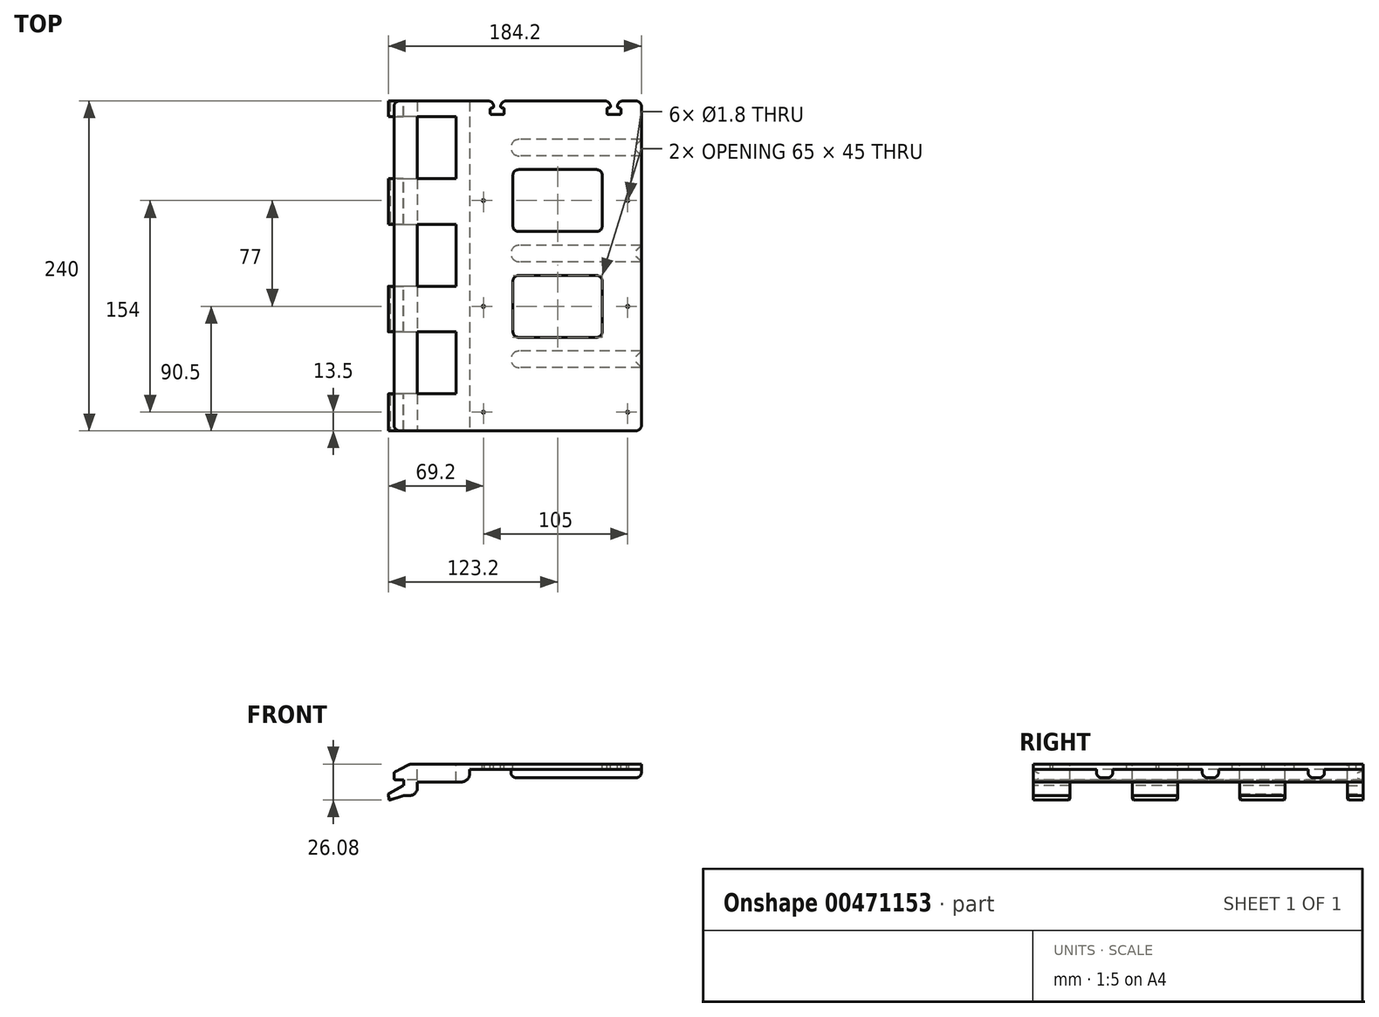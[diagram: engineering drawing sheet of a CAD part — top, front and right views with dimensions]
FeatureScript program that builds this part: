
annotation { "Feature Type Name" : "Feature", "Feature Type Description" : "" }
export const myFeature = defineFeature(function(context is Context, id is Id, definition is map)
    precondition{}
    {
        {
            var Q0;
            Q0=qCreatedBy(makeId("Top.planeOp"),FACE);
            var sketch = newSketch(context, id + "F0", { "sketchPlane" : qUnion([Q0])});
            skLineSegment(sketch, "E0", {"start": v(0, -188) * mm, "end": v(180, -188) * mm, "construction": true});
            skLineSegment(sketch, "E1", {"start": v(0, -34) * mm, "end": v(180, -34) * mm, "construction": true});
            skLineSegment(sketch, "E2", {"start": v(0, -149.5) * mm, "end": v(180, -149.5) * mm, "construction": true});
            skLineSegment(sketch, "E3", {"start": v(0, -72.5) * mm, "end": v(180, -72.5) * mm, "construction": true});
            skLineSegment(sketch, "E4", {"start": v(180, -194) * mm, "end": v(91, -194) * mm});
            skLineSegment(sketch, "E5", {"start": v(180, -182) * mm, "end": v(91, -182) * mm});
            skArc(sketch, "E6", {"start": v(91, -182) * mm, "mid": v(85, -188) * mm, "end": v(91, -194) * mm});
            skLineSegment(sketch, "E7", {"start": v(180, -117) * mm, "end": v(91, -117) * mm});
            skLineSegment(sketch, "E8", {"start": v(180, -105) * mm, "end": v(91, -105) * mm});
            skArc(sketch, "E9", {"start": v(91, -105) * mm, "mid": v(85, -111) * mm, "end": v(91, -117) * mm});
            skLineSegment(sketch, "E10", {"start": v(180, -40) * mm, "end": v(91, -40) * mm});
            skLineSegment(sketch, "E11", {"start": v(180, -28) * mm, "end": v(91, -28) * mm});
            skArc(sketch, "E12", {"start": v(91, -28) * mm, "mid": v(85, -34) * mm, "end": v(91, -40) * mm});
            skLineSegment(sketch, "E13", {"start": v(91, -240) * mm, "end": v(91, 0) * mm, "construction": true});
            skCircle(sketch, "E14", {"center": v(65, -149.5) * mm, "radius": 0.9 * mm});
            skCircle(sketch, "E15", {"center": v(65, -72.5) * mm, "radius": 0.9 * mm});
            skCircle(sketch, "E16", {"center": v(170, -149.5) * mm, "radius": 0.9 * mm});
            skCircle(sketch, "E17", {"center": v(170, -72.5) * mm, "radius": 0.9 * mm});
            skLineSegment(sketch, "E18.bottom", {"start": v(180, -240) * mm, "end": v(0, -240) * mm});
            skLineSegment(sketch, "E18.top", {"start": v(180, 0) * mm, "end": v(0, 0) * mm});
            skLineSegment(sketch, "E18.left", {"start": v(180, -240) * mm, "end": v(180, 0) * mm});
            skLineSegment(sketch, "E18.right", {"start": v(0, -240) * mm, "end": v(0, 0) * mm});
            skLineSegment(sketch, "E19", {"start": v(5, 0) * mm, "end": v(5, -240) * mm});
            skLineSegment(sketch, "E20", {"start": v(17, 0) * mm, "end": v(17, -240) * mm});
            skLineSegment(sketch, "E21", {"start": v(55, 0) * mm, "end": v(55, -240) * mm});
            skLineSegment(sketch, "E22", {"start": v(0, -89.7) * mm, "end": v(45, -89.7) * mm});
            skLineSegment(sketch, "E23", {"start": v(45, -89.7) * mm, "end": v(45, -134.9) * mm});
            skLineSegment(sketch, "E24", {"start": v(45, -134.9) * mm, "end": v(0, -134.9) * mm});
            skLineSegment(sketch, "E25", {"start": v(0, -168) * mm, "end": v(45, -168) * mm});
            skLineSegment(sketch, "E26", {"start": v(45, -168) * mm, "end": v(45, -213.2) * mm});
            skLineSegment(sketch, "E27", {"start": v(45, -213.2) * mm, "end": v(0, -213.2) * mm});
            skLineSegment(sketch, "E28", {"start": v(0, -56.6) * mm, "end": v(45, -56.6) * mm});
            skLineSegment(sketch, "E29", {"start": v(45, -56.6) * mm, "end": v(45, -11.4) * mm});
            skLineSegment(sketch, "E30", {"start": v(45, -11.4) * mm, "end": v(0, -11.4) * mm});
            skLineSegment(sketch, "E31", {"start": v(0, -226.5) * mm, "end": v(180, -226.5) * mm, "construction": true});
            skCircle(sketch, "E32", {"center": v(65, -226.5) * mm, "radius": 0.9 * mm});
            skCircle(sketch, "E33", {"center": v(170, -226.5) * mm, "radius": 0.9 * mm});
            skLineSegment(sketch, "E34.bottom", {"start": v(151.5, -95) * mm, "end": v(86.5, -95) * mm});
            skLineSegment(sketch, "E34.top", {"start": v(151.5, -50) * mm, "end": v(86.5, -50) * mm});
            skLineSegment(sketch, "E34.left", {"start": v(151.5, -95) * mm, "end": v(151.5, -50) * mm});
            skLineSegment(sketch, "E34.right", {"start": v(86.5, -95) * mm, "end": v(86.5, -50) * mm});
            skPoint(sketch, "E34.middle", {"position": v(119, -72.5) * mm});
            skLineSegment(sketch, "E35.bottom", {"start": v(151.5, -172) * mm, "end": v(86.5, -172) * mm});
            skLineSegment(sketch, "E35.top", {"start": v(151.5, -127) * mm, "end": v(86.5, -127) * mm});
            skLineSegment(sketch, "E35.left", {"start": v(151.5, -172) * mm, "end": v(151.5, -127) * mm});
            skLineSegment(sketch, "E35.right", {"start": v(86.5, -172) * mm, "end": v(86.5, -127) * mm});
            skPoint(sketch, "E35.middle", {"position": v(119, -149.5) * mm});
            skPoint(sketch, "E36.centerSnap0", {"position": v(119, -172) * mm});
            skLineSegment(sketch, "E37", {"start": v(91, -111) * mm, "end": v(180, -111) * mm, "construction": true});
            skLineSegment(sketch, "E38", {"start": v(91, -111) * mm, "end": v(0, -111) * mm, "construction": true});
            skLineSegment(sketch, "E39.bottom", {"start": v(157.5, 0) * mm, "end": v(162.5, 0) * mm});
            skLineSegment(sketch, "E39.top", {"start": v(157.5, -5) * mm, "end": v(162.5, -5) * mm});
            skLineSegment(sketch, "E39.left", {"start": v(157.5, 0) * mm, "end": v(157.5, -5) * mm});
            skLineSegment(sketch, "E39.right", {"start": v(162.5, 0) * mm, "end": v(162.5, -5) * mm});
            skLineSegment(sketch, "E40.bottom", {"start": v(72.5, 0) * mm, "end": v(77.5, 0) * mm});
            skLineSegment(sketch, "E40.top", {"start": v(72.5, -5) * mm, "end": v(77.5, -5) * mm});
            skLineSegment(sketch, "E40.left", {"start": v(72.5, 0) * mm, "end": v(72.5, -5) * mm});
            skLineSegment(sketch, "E40.right", {"start": v(77.5, 0) * mm, "end": v(77.5, -5) * mm});
            skLineSegment(sketch, "E41", {"start": v(75, -5) * mm, "end": v(75, -34) * mm, "construction": true});
            skLineSegment(sketch, "E42", {"start": v(160, -5) * mm, "end": v(160, -34) * mm, "construction": true});
            skLineSegment(sketch, "E43.bottom", {"start": v(70, -5) * mm, "end": v(80, -5) * mm});
            skLineSegment(sketch, "E43.top", {"start": v(70, -10) * mm, "end": v(80, -10) * mm});
            skLineSegment(sketch, "E43.left", {"start": v(70, -5) * mm, "end": v(70, -10) * mm});
            skLineSegment(sketch, "E43.right", {"start": v(80, -5) * mm, "end": v(80, -10) * mm});
            skLineSegment(sketch, "E44.bottom", {"start": v(155, -5) * mm, "end": v(165, -5) * mm});
            skLineSegment(sketch, "E44.top", {"start": v(155, -10) * mm, "end": v(165, -10) * mm});
            skLineSegment(sketch, "E44.left", {"start": v(155, -5) * mm, "end": v(155, -10) * mm});
            skLineSegment(sketch, "E44.right", {"start": v(165, -5) * mm, "end": v(165, -10) * mm});
            skLineSegment(sketch, "E45.bottom", {"start": v(152.5, -240) * mm, "end": v(147.5, -240) * mm});
            skSolve(sketch);
        }
        {
            var Q0;
            {var subQ7=sQuery(id+"F0.wireOp",EDGE,"E4");Q0=makeQuery(id+"F0.imprint","IMPRINT",FACE,{"disambiguationData":[TD([[makeQuery(id+"F0.imprint","IMPRINT",EDGE,{"derivedFrom":subQ7}),1.0]])]});}
            var Q1;
            {var subQ0=sQuery(id+"F0.wireOp",EDGE,"E4");Q1=makeQuery(id+"F0.imprint","IMPRINT",FACE,{"disambiguationData":[TD([[makeQuery(id+"F0.imprint","IMPRINT",EDGE,{"derivedFrom":subQ0}),-1.0]])]});}
            var Q2;
            {var subQ0=sQuery(id+"F0.wireOp",EDGE,"E7");Q2=makeQuery(id+"F0.imprint","IMPRINT",FACE,{"disambiguationData":[TD([[makeQuery(id+"F0.imprint","IMPRINT",EDGE,{"derivedFrom":subQ0}),-1.0]])]});}
            var Q3;
            {var subQ0=sQuery(id+"F0.wireOp",EDGE,"E10");Q3=makeQuery(id+"F0.imprint","IMPRINT",FACE,{"disambiguationData":[TD([[makeQuery(id+"F0.imprint","IMPRINT",EDGE,{"derivedFrom":subQ0}),-1.0]])]});}
            extrude(context, id + "F1", {"entities" : qUnion([Q0, Q1, Q2, Q3]), "oppositeDirection" : true, "depth" : 4 * mm});
        }
        {
            var Q0;
            {var subQ0=sQuery(id+"F0.wireOp",EDGE,"E20");Q0=makeQuery(id+"F0.imprint","IMPRINT",FACE,{"disambiguationData":[TD([[makeQuery(id+"F0.imprint","IMPRINT",EDGE,{"derivedFrom":subQ0}),1.0]])]});}
            var Q1;
            {var subQ5=sQuery(id+"F0.wireOp",EDGE,"n4lQ4PQO-9XsQ-tz0W-XekK-HpTfJCge4sbG");Q1=makeQuery(id+"F0.imprint","IMPRINT",FACE,{"disambiguationData":[TD([[makeQuery(id+"F0.imprint","IMPRINT",EDGE,{"derivedFrom":subQ5}),1.0]])]});}
            var Q2;
            {var subQ5=sQuery(id+"F0.wireOp",EDGE,"NRY2d1nv-D3un-2PJu-Z2eF-jLOu5DY2E8th");Q2=makeQuery(id+"F0.imprint","IMPRINT",FACE,{"disambiguationData":[TD([[makeQuery(id+"F0.imprint","IMPRINT",EDGE,{"derivedFrom":subQ5}),1.0]])]});}
            extrude(context, id + "F2", {"entities" : qUnion([Q0, Q1, Q2]), "operationType" : NewBodyOperationType.ADD, "oppositeDirection" : true, "depth" : 13 * mm});
        }
        {
            var Q0;
            {var subQ0=sQuery(id+"F0.wireOp",EDGE,"E19");var subQ1=sQuery(id+"F0.wireOp",EDGE,"E18.bottom");var subQ2=makeQuery(id+"F0.imprint","INTERSECT",VERTEX,{"derivedFrom":[subQ1,subQ0]});Q0=makeQuery(id+"F0.imprint","IMPRINT",FACE,{"disambiguationData":[TD([[makeQuery(id+"F0.imprint","IMPRINT",EDGE,{"disambiguationData":[TD([[subQ2,1.0]])],"derivedFrom":subQ1}),-1.0]])]});}
            var Q1;
            {var subQ0=sQuery(id+"F0.wireOp",EDGE,"E19");var subQ1=sQuery(id+"F0.wireOp",EDGE,"E18.top");var subQ2=makeQuery(id+"F0.imprint","INTERSECT",VERTEX,{"derivedFrom":[subQ1,subQ0]});Q1=makeQuery(id+"F0.imprint","IMPRINT",FACE,{"disambiguationData":[TD([[makeQuery(id+"F0.imprint","IMPRINT",EDGE,{"disambiguationData":[TD([[subQ2,1.0]])],"derivedFrom":subQ1}),1.0]])]});}
            var Q2;
            {var subQ0=sQuery(id+"F0.wireOp",EDGE,"E28");var subQ1=sQuery(id+"F0.wireOp",EDGE,"E19");var subQ2=makeQuery(id+"F0.imprint","INTERSECT",VERTEX,{"derivedFrom":[subQ1,subQ0]});Q2=makeQuery(id+"F0.imprint","IMPRINT",FACE,{"disambiguationData":[TD([[makeQuery(id+"F0.imprint","IMPRINT",EDGE,{"disambiguationData":[TD([[subQ2,-1.0]])],"derivedFrom":subQ1}),1.0]])]});}
            var Q3;
            {var subQ0=sQuery(id+"F0.wireOp",EDGE,"E24");var subQ1=sQuery(id+"F0.wireOp",EDGE,"E19");var subQ2=makeQuery(id+"F0.imprint","INTERSECT",VERTEX,{"derivedFrom":[subQ1,subQ0]});Q3=makeQuery(id+"F0.imprint","IMPRINT",FACE,{"disambiguationData":[TD([[makeQuery(id+"F0.imprint","IMPRINT",EDGE,{"disambiguationData":[TD([[subQ2,-1.0]])],"derivedFrom":subQ1}),1.0]])]});}
            extrude(context, id + "F3", {"entities" : qUnion([Q0, Q1, Q2, Q3]), "operationType" : NewBodyOperationType.ADD, "oppositeDirection" : true, "depth" : 23 * mm});
        }
        {
            var Q0;
            {var subQ0=sQuery(id+"F0.wireOp",EDGE,"E18.right");var subQ1=sQuery(id+"F0.wireOp",EDGE,"E18.bottom");var subQ2=makeQuery(id+"F0.imprint","INTERSECT",VERTEX,{"derivedFrom":[subQ1,subQ0]});Q0=makeQuery(id+"F0.imprint","IMPRINT",FACE,{"disambiguationData":[TD([[makeQuery(id+"F0.imprint","IMPRINT",EDGE,{"disambiguationData":[TD([[subQ2,1.0]])],"derivedFrom":subQ1}),-1.0]])]});}
            var Q1;
            {var subQ0=sQuery(id+"F0.wireOp",EDGE,"E18.right");var subQ1=sQuery(id+"F0.wireOp",EDGE,"E18.top");var subQ2=makeQuery(id+"F0.imprint","INTERSECT",VERTEX,{"derivedFrom":[subQ1,subQ0]});Q1=makeQuery(id+"F0.imprint","IMPRINT",FACE,{"disambiguationData":[TD([[makeQuery(id+"F0.imprint","IMPRINT",EDGE,{"disambiguationData":[TD([[subQ2,1.0]])],"derivedFrom":subQ1}),1.0]])]});}
            var Q2;
            {var subQ0=sQuery(id+"F0.wireOp",EDGE,"E24");var subQ1=sQuery(id+"F0.wireOp",EDGE,"E18.right");var subQ2=makeQuery(id+"F0.imprint","INTERSECT",VERTEX,{"derivedFrom":[subQ1,subQ0]});Q2=makeQuery(id+"F0.imprint","IMPRINT",FACE,{"disambiguationData":[TD([[makeQuery(id+"F0.imprint","IMPRINT",EDGE,{"disambiguationData":[TD([[subQ2,1.0]])],"derivedFrom":subQ1}),-1.0]])]});}
            var Q3;
            {var subQ0=sQuery(id+"F0.wireOp",EDGE,"E22");var subQ1=sQuery(id+"F0.wireOp",EDGE,"E18.right");var subQ2=makeQuery(id+"F0.imprint","INTERSECT",VERTEX,{"derivedFrom":[subQ1,subQ0]});Q3=makeQuery(id+"F0.imprint","IMPRINT",FACE,{"disambiguationData":[TD([[makeQuery(id+"F0.imprint","IMPRINT",EDGE,{"disambiguationData":[TD([[subQ2,-1.0]])],"derivedFrom":subQ1}),-1.0]])]});}
            var Q4;
            {var subQ0=sQuery(id+"F0.wireOp",EDGE,"E25");var subQ1=sQuery(id+"F0.wireOp",EDGE,"E18.right");var subQ2=makeQuery(id+"F0.imprint","INTERSECT",VERTEX,{"derivedFrom":[subQ1,subQ0]});Q4=makeQuery(id+"F0.imprint","IMPRINT",FACE,{"disambiguationData":[TD([[makeQuery(id+"F0.imprint","IMPRINT",EDGE,{"disambiguationData":[TD([[subQ2,1.0]])],"derivedFrom":subQ1}),-1.0]])]});}
            var Q5;
            {var subQ0=sQuery(id+"F0.wireOp",EDGE,"E22");var subQ1=sQuery(id+"F0.wireOp",EDGE,"E18.right");var subQ2=makeQuery(id+"F0.imprint","INTERSECT",VERTEX,{"derivedFrom":[subQ1,subQ0]});Q5=makeQuery(id+"F0.imprint","IMPRINT",FACE,{"disambiguationData":[TD([[makeQuery(id+"F0.imprint","IMPRINT",EDGE,{"disambiguationData":[TD([[subQ2,1.0]])],"derivedFrom":subQ1}),-1.0]])]});}
            var Q6;
            {var subQ0=sQuery(id+"F0.wireOp",EDGE,"E28");var subQ1=sQuery(id+"F0.wireOp",EDGE,"E18.right");var subQ2=makeQuery(id+"F0.imprint","INTERSECT",VERTEX,{"derivedFrom":[subQ1,subQ0]});Q6=makeQuery(id+"F0.imprint","IMPRINT",FACE,{"disambiguationData":[TD([[makeQuery(id+"F0.imprint","IMPRINT",EDGE,{"disambiguationData":[TD([[subQ2,-1.0]])],"derivedFrom":subQ1}),-1.0]])]});}
            var Q7;
            {var subQ0=sQuery(id+"F0.wireOp",EDGE,"E25");var subQ1=sQuery(id+"F0.wireOp",EDGE,"E19");var subQ2=makeQuery(id+"F0.imprint","INTERSECT",VERTEX,{"derivedFrom":[subQ1,subQ0]});Q7=makeQuery(id+"F0.imprint","IMPRINT",FACE,{"disambiguationData":[TD([[makeQuery(id+"F0.imprint","IMPRINT",EDGE,{"disambiguationData":[TD([[subQ2,-1.0]])],"derivedFrom":subQ1}),1.0]])]});}
            var Q8;
            {var subQ0=sQuery(id+"F0.wireOp",EDGE,"E22");var subQ1=sQuery(id+"F0.wireOp",EDGE,"E19");var subQ2=makeQuery(id+"F0.imprint","INTERSECT",VERTEX,{"derivedFrom":[subQ1,subQ0]});Q8=makeQuery(id+"F0.imprint","IMPRINT",FACE,{"disambiguationData":[TD([[makeQuery(id+"F0.imprint","IMPRINT",EDGE,{"disambiguationData":[TD([[subQ2,-1.0]])],"derivedFrom":subQ1}),1.0]])]});}
            var Q9;
            {var subQ0=sQuery(id+"F0.wireOp",EDGE,"E30");var subQ1=sQuery(id+"F0.wireOp",EDGE,"E19");var subQ2=makeQuery(id+"F0.imprint","INTERSECT",VERTEX,{"derivedFrom":[subQ1,subQ0]});Q9=makeQuery(id+"F0.imprint","IMPRINT",FACE,{"disambiguationData":[TD([[makeQuery(id+"F0.imprint","IMPRINT",EDGE,{"disambiguationData":[TD([[subQ2,-1.0]])],"derivedFrom":subQ1}),1.0]])]});}
            var Q10;
            Q10=makeQuery(id+"F2.opExtrude","CAP_FACE",FACE,{"disambiguationData":[OSD([sQuery(id+"F0.wireOp",EDGE,"E14"),sQuery(id+"F0.wireOp",EDGE,"E15"),sQuery(id+"F0.wireOp",EDGE,"E18.bottom"),sQuery(id+"F0.wireOp",EDGE,"E18.top"),sQuery(id+"F0.wireOp",EDGE,"E20"),sQuery(id+"F0.wireOp",EDGE,"E21")])],"isStart":false});
            extrude(context, id + "F4", {"entities" : qUnion([Q0, Q1, Q2, Q3, Q4, Q5, Q6, Q7, Q8, Q9]), "operationType" : NewBodyOperationType.ADD, "oppositeDirection" : true, "endBoundEntityFace" : qUnion([Q10]), "depth" : 11.5 * mm});
        }
        {
            var Q0;
            {var subQ0=sQuery(id+"F0.wireOp",EDGE,"E18.bottom");Q0=makeQuery(id+"F4.boolean.opBoolean","MERGE",FACE,{"derivedFrom":[makeQuery(id+"F3.boolean.opBoolean","MERGE",FACE,{"derivedFrom":[makeQuery(id+"F2.boolean.opBoolean","MERGE",FACE,{"derivedFrom":[makeQuery(id+"F1.opExtrude","SWEPT_FACE",FACE,{"disambiguationData":[OSD([subQ0])]}),makeQuery(id+"F2.opExtrude","SWEPT_FACE",FACE,{"disambiguationData":[OSD([subQ0])]})]}),makeQuery(id+"F3.opExtrude","SWEPT_FACE",FACE,{"disambiguationData":[OSD([subQ0])]})]}),makeQuery(id+"F4.opExtrude","SWEPT_FACE",FACE,{"disambiguationData":[OSD([subQ0])]})]});}
            var sketch = newSketch(context, id + "F5", { "sketchPlane" : qUnion([Q0])});
            skLineSegment(sketch, "E46.bottom", {"start": v(5, -11.5) * mm, "end": v(7, -11.5) * mm});
            skLineSegment(sketch, "E46.top", {"start": v(5, -15.5) * mm, "end": v(7, -15.5) * mm});
            skLineSegment(sketch, "E46.left", {"start": v(5, -11.5) * mm, "end": v(5, -15.5) * mm});
            skLineSegment(sketch, "E46.right", {"start": v(7, -11.5) * mm, "end": v(7, -15.5) * mm});
            skSolve(sketch);
        }
        {
            var Q0;
            Q0=makeQuery(id+"F5.imprint","IMPRINT",FACE,{"disambiguationData":[TD([[makeQuery(id+"F5.imprint","IMPRINT",EDGE,{"derivedFrom":sQuery(id+"F5.wireOp",EDGE,"E46.bottom")}),-1.0]])]});
            var Q1;
            {var subQ0=sQuery(id+"F0.wireOp",EDGE,"E18.top");Q1=makeQuery(id+"F4.boolean.opBoolean","MERGE",FACE,{"derivedFrom":[makeQuery(id+"F3.boolean.opBoolean","MERGE",FACE,{"derivedFrom":[makeQuery(id+"F2.boolean.opBoolean","MERGE",FACE,{"derivedFrom":[makeQuery(id+"F1.opExtrude","SWEPT_FACE",FACE,{"disambiguationData":[OSD([subQ0])]}),makeQuery(id+"F2.opExtrude","SWEPT_FACE",FACE,{"disambiguationData":[OSD([subQ0])]})]}),makeQuery(id+"F3.opExtrude","SWEPT_FACE",FACE,{"disambiguationData":[OSD([subQ0])]})]}),makeQuery(id+"F4.opExtrude","SWEPT_FACE",FACE,{"disambiguationData":[OSD([subQ0])]})]});}
            extrude(context, id + "F6", {"entities" : qUnion([Q0]), "operationType" : NewBodyOperationType.REMOVE, "oppositeDirection" : true, "endBoundEntityFace" : qUnion([Q1]), "depth" : 300 * mm});
        }
        {
            var Q0;
            {var subQ0=sQuery(id+"F0.wireOp",EDGE,"E4");Q0=makeQuery(id+"F0.imprint","IMPRINT",FACE,{"disambiguationData":[TD([[makeQuery(id+"F0.imprint","IMPRINT",EDGE,{"derivedFrom":subQ0}),-1.0]])]});}
            var Q1;
            {var subQ0=sQuery(id+"F0.wireOp",EDGE,"E7");Q1=makeQuery(id+"F0.imprint","IMPRINT",FACE,{"disambiguationData":[TD([[makeQuery(id+"F0.imprint","IMPRINT",EDGE,{"derivedFrom":subQ0}),-1.0]])]});}
            var Q2;
            {var subQ0=sQuery(id+"F0.wireOp",EDGE,"E10");Q2=makeQuery(id+"F0.imprint","IMPRINT",FACE,{"disambiguationData":[TD([[makeQuery(id+"F0.imprint","IMPRINT",EDGE,{"derivedFrom":subQ0}),-1.0]])]});}
            extrude(context, id + "F7", {"entities" : qUnion([Q0, Q1, Q2]), "operationType" : NewBodyOperationType.ADD, "oppositeDirection" : true, "depth" : 10 * mm});
        }
        {
            var Q0;
            Q0=makeQuery(id+"F7.opExtrude","CAP_FACE",FACE,{"disambiguationData":[OSD([sQuery(id+"F0.wireOp",EDGE,"E10"),sQuery(id+"F0.wireOp",EDGE,"E11"),sQuery(id+"F0.wireOp",EDGE,"E12"),sQuery(id+"F0.wireOp",EDGE,"E18.left")])],"isStart":false});
            var Q1;
            Q1=makeQuery(id+"F7.opExtrude","CAP_FACE",FACE,{"disambiguationData":[OSD([sQuery(id+"F0.wireOp",EDGE,"E7"),sQuery(id+"F0.wireOp",EDGE,"E8"),sQuery(id+"F0.wireOp",EDGE,"E9"),sQuery(id+"F0.wireOp",EDGE,"E18.left")])],"isStart":false});
            var Q2;
            Q2=makeQuery(id+"F7.opExtrude","CAP_FACE",FACE,{"disambiguationData":[OSD([sQuery(id+"F0.wireOp",EDGE,"E4"),sQuery(id+"F0.wireOp",EDGE,"E5"),sQuery(id+"F0.wireOp",EDGE,"E6"),sQuery(id+"F0.wireOp",EDGE,"E18.left")])],"isStart":false});
            var Q3;
            Q3=makeQuery(id+"F1.opExtrude","SWEPT_EDGE",EDGE,{"disambiguationData":[OSD([sQuery(id+"F0.wireOp",EDGE,"E34.top"),sQuery(id+"F0.wireOp",EDGE,"E34.right")])]});
            var Q4;
            Q4=makeQuery(id+"F1.opExtrude","SWEPT_EDGE",EDGE,{"disambiguationData":[OSD([sQuery(id+"F0.wireOp",EDGE,"E34.bottom"),sQuery(id+"F0.wireOp",EDGE,"E34.right")])]});
            var Q5;
            Q5=makeQuery(id+"F1.opExtrude","SWEPT_EDGE",EDGE,{"disambiguationData":[OSD([sQuery(id+"F0.wireOp",EDGE,"E34.top"),sQuery(id+"F0.wireOp",EDGE,"E34.left")])]});
            var Q6;
            Q6=makeQuery(id+"F1.opExtrude","SWEPT_EDGE",EDGE,{"disambiguationData":[OSD([sQuery(id+"F0.wireOp",EDGE,"E34.bottom"),sQuery(id+"F0.wireOp",EDGE,"E34.left")])]});
            var Q7;
            Q7=makeQuery(id+"F1.opExtrude","SWEPT_EDGE",EDGE,{"disambiguationData":[OSD([sQuery(id+"F0.wireOp",EDGE,"E35.top"),sQuery(id+"F0.wireOp",EDGE,"E35.left")])]});
            var Q8;
            {var subQ0=sQuery(id+"F0.wireOp",EDGE,"E36");var subQ1=sQuery(id+"F0.wireOp",EDGE,"E18.bottom");Q8=makeQuery(id+"F1.opExtrude","SWEPT_EDGE",EDGE,{"disambiguationData":[OSD([subQ1,subQ0]),TDD([makeQuery(id+"F0.imprint","INTERSECT",VERTEX,{"disambiguationData":[OD(1.0)],"derivedFrom":[subQ1,subQ0]})])]});}
            var Q9;
            Q9=makeQuery(id+"F1.opExtrude","SWEPT_EDGE",EDGE,{"disambiguationData":[OSD([sQuery(id+"F0.wireOp",EDGE,"E35.bottom"),sQuery(id+"F0.wireOp",EDGE,"E35.right")])]});
            var Q10;
            Q10=makeQuery(id+"F1.opExtrude","SWEPT_EDGE",EDGE,{"disambiguationData":[OSD([sQuery(id+"F0.wireOp",EDGE,"E35.top"),sQuery(id+"F0.wireOp",EDGE,"E35.right")])]});
            var Q11;
            {var subQ0=sQuery(id+"F0.wireOp",EDGE,"dDL4M1PI-aelY-u7zt-lnq0-sMzwrNtlq2yo");var subQ1=sQuery(id+"F0.wireOp",EDGE,"E18.top");Q11=makeQuery(id+"F1.opExtrude","SWEPT_EDGE",EDGE,{"disambiguationData":[OSD([subQ1,subQ0]),TDD([makeQuery(id+"F0.imprint","INTERSECT",VERTEX,{"disambiguationData":[OD(1.0)],"derivedFrom":[subQ1,subQ0]})])]});}
            var Q12;
            {var subQ0=sQuery(id+"F0.wireOp",EDGE,"dDL4M1PI-aelY-u7zt-lnq0-sMzwrNtlq2yo");var subQ1=sQuery(id+"F0.wireOp",EDGE,"E18.top");Q12=makeQuery(id+"F1.opExtrude","SWEPT_EDGE",EDGE,{"disambiguationData":[OSD([subQ1,subQ0]),TDD([makeQuery(id+"F0.imprint","INTERSECT",VERTEX,{"disambiguationData":[OD(0.0)],"derivedFrom":[subQ1,subQ0]})])]});}
            var Q13;
            Q13=makeQuery(id+"F1.opExtrude","SWEPT_EDGE",EDGE,{"disambiguationData":[OSD([sQuery(id+"F0.wireOp",EDGE,"E35.bottom"),sQuery(id+"F0.wireOp",EDGE,"E35.left")])]});
            var Q14;
            {var subQ0=sQuery(id+"F0.wireOp",EDGE,"E36");var subQ1=sQuery(id+"F0.wireOp",EDGE,"E18.bottom");Q14=makeQuery(id+"F1.opExtrude","SWEPT_EDGE",EDGE,{"disambiguationData":[OSD([subQ1,subQ0]),TDD([makeQuery(id+"F0.imprint","INTERSECT",VERTEX,{"disambiguationData":[OD(0.0)],"derivedFrom":[subQ1,subQ0]})])]});}
            var Q15;
            Q15=makeQuery(id+"F1.opExtrude","SWEPT_EDGE",EDGE,{"disambiguationData":[OSD([sQuery(id+"F0.wireOp",EDGE,"E18.bottom"),sQuery(id+"F0.wireOp",EDGE,"E18.left")])]});
            var Q16;
            Q16=makeQuery(id+"F1.opExtrude","SWEPT_EDGE",EDGE,{"disambiguationData":[OSD([sQuery(id+"F0.wireOp",EDGE,"E18.top"),sQuery(id+"F0.wireOp",EDGE,"E18.left")])]});
            var Q17;
            Q17=makeQuery(id+"F4.opExtrude","SWEPT_EDGE",EDGE,{"disambiguationData":[OSD([sQuery(id+"F0.wireOp",EDGE,"E18.top"),sQuery(id+"F0.wireOp",EDGE,"E18.right")])]});
            var Q18;
            Q18=makeQuery(id+"F4.opExtrude","SWEPT_EDGE",EDGE,{"disambiguationData":[OSD([sQuery(id+"F0.wireOp",EDGE,"E18.bottom"),sQuery(id+"F0.wireOp",EDGE,"E18.right")])]});
            fillet(context, id + "F8", {"entities" : qUnion([Q0, Q1, Q2, Q3, Q4, Q5, Q6, Q7, Q8, Q9, Q10, Q11, Q12, Q13, Q14, Q15, Q16, Q17, Q18]), "radius" : 4 * mm, "tangentPropagation" : true, "allowEdgeOverflow" : false});
        }
        {
            var Q0;
            Q0=makeQuery(id+"F4.opExtrude","CAP_EDGE",EDGE,{"disambiguationData":[OSD([sQuery(id+"F0.wireOp",EDGE,"E18.right")])],"isStart":true});
            chamfer(context, id + "F9", {"entities" : qUnion([Q0]), "chamferType" : ChamferType.TWO_OFFSETS, "width1" : 6 * mm, "oppositeDirection" : false, "width2" : 12 * mm});
        }
        {
            var Q0;
            {var subQ0=sQuery(id+"F0.wireOp",EDGE,"E19");Q0=makeQuery(id+"F3.opExtrude","CAP_EDGE",EDGE,{"disambiguationData":[OSD([subQ0]),TDD([makeQuery(id+"F0.imprint","IMPRINT",EDGE,{"disambiguationData":[TD([[makeQuery(id+"F0.imprint","INTERSECT",VERTEX,{"derivedFrom":[sQuery(id+"F0.wireOp",EDGE,"E18.bottom"),subQ0]}),1.0]])],"derivedFrom":subQ0})])],"isStart":false});}
            var Q1;
            {var subQ0=sQuery(id+"F0.wireOp",EDGE,"E19");Q1=makeQuery(id+"F3.opExtrude","CAP_EDGE",EDGE,{"disambiguationData":[OSD([subQ0]),TDD([makeQuery(id+"F0.imprint","IMPRINT",EDGE,{"disambiguationData":[TD([[makeQuery(id+"F0.imprint","INTERSECT",VERTEX,{"derivedFrom":[subQ0,sQuery(id+"F0.wireOp",EDGE,"E24")]}),-1.0]])],"derivedFrom":subQ0})])],"isStart":false});}
            var Q2;
            {var subQ0=sQuery(id+"F0.wireOp",EDGE,"E19");Q2=makeQuery(id+"F3.opExtrude","CAP_EDGE",EDGE,{"disambiguationData":[OSD([subQ0]),TDD([makeQuery(id+"F0.imprint","IMPRINT",EDGE,{"disambiguationData":[TD([[makeQuery(id+"F0.imprint","INTERSECT",VERTEX,{"derivedFrom":[subQ0,sQuery(id+"F0.wireOp",EDGE,"E28")]}),-1.0]])],"derivedFrom":subQ0})])],"isStart":false});}
            var Q3;
            {var subQ0=sQuery(id+"F0.wireOp",EDGE,"E19");Q3=makeQuery(id+"F3.opExtrude","CAP_EDGE",EDGE,{"disambiguationData":[OSD([subQ0]),TDD([makeQuery(id+"F0.imprint","IMPRINT",EDGE,{"disambiguationData":[TD([[makeQuery(id+"F0.imprint","INTERSECT",VERTEX,{"derivedFrom":[sQuery(id+"F0.wireOp",EDGE,"E18.top"),subQ0]}),-1.0]])],"derivedFrom":subQ0})])],"isStart":false});}
            chamfer(context, id + "F10", {"entities" : qUnion([Q0, Q1, Q2, Q3]), "chamferType" : ChamferType.TWO_OFFSETS, "width1" : 20 * mm, "oppositeDirection" : false, "width2" : 2 * mm});
        }
        {
            var Q0;
            {var subQ0=sQuery(id+"F0.wireOp",EDGE,"E19");Q0=makeQuery(id+"F10.opChamfer","BLEND_FACE",FACE,{"disambiguationData":[OSD([subQ0]),TDD([makeQuery(id+"F3.opExtrude","CAP_EDGE",EDGE,{"disambiguationData":[OSD([subQ0]),TDD([makeQuery(id+"F0.imprint","IMPRINT",EDGE,{"disambiguationData":[TD([[makeQuery(id+"F0.imprint","INTERSECT",VERTEX,{"derivedFrom":[sQuery(id+"F0.wireOp",EDGE,"E18.bottom"),subQ0]}),1.0]])],"derivedFrom":subQ0})])],"isStart":false})])]});}
            var Q1;
            {var subQ0=sQuery(id+"F0.wireOp",EDGE,"E19");Q1=makeQuery(id+"F10.opChamfer","BLEND_FACE",FACE,{"disambiguationData":[OSD([subQ0]),TDD([makeQuery(id+"F3.opExtrude","CAP_EDGE",EDGE,{"disambiguationData":[OSD([subQ0]),TDD([makeQuery(id+"F0.imprint","IMPRINT",EDGE,{"disambiguationData":[TD([[makeQuery(id+"F0.imprint","INTERSECT",VERTEX,{"derivedFrom":[subQ0,sQuery(id+"F0.wireOp",EDGE,"E24")]}),-1.0]])],"derivedFrom":subQ0})])],"isStart":false})])]});}
            var Q2;
            {var subQ0=sQuery(id+"F0.wireOp",EDGE,"E19");Q2=makeQuery(id+"F10.opChamfer","BLEND_FACE",FACE,{"disambiguationData":[OSD([subQ0]),TDD([makeQuery(id+"F3.opExtrude","CAP_EDGE",EDGE,{"disambiguationData":[OSD([subQ0]),TDD([makeQuery(id+"F0.imprint","IMPRINT",EDGE,{"disambiguationData":[TD([[makeQuery(id+"F0.imprint","INTERSECT",VERTEX,{"derivedFrom":[subQ0,sQuery(id+"F0.wireOp",EDGE,"E28")]}),-1.0]])],"derivedFrom":subQ0})])],"isStart":false})])]});}
            var Q3;
            {var subQ0=sQuery(id+"F0.wireOp",EDGE,"E19");Q3=makeQuery(id+"F10.opChamfer","BLEND_FACE",FACE,{"disambiguationData":[OSD([subQ0]),TDD([makeQuery(id+"F3.opExtrude","CAP_EDGE",EDGE,{"disambiguationData":[OSD([subQ0]),TDD([makeQuery(id+"F0.imprint","IMPRINT",EDGE,{"disambiguationData":[TD([[makeQuery(id+"F0.imprint","INTERSECT",VERTEX,{"derivedFrom":[sQuery(id+"F0.wireOp",EDGE,"E18.top"),subQ0]}),-1.0]])],"derivedFrom":subQ0})])],"isStart":false})])]});}
            extrude(context, id + "F11", {"entities" : qUnion([Q0, Q1, Q2, Q3]), "operationType" : NewBodyOperationType.ADD, "depth" : 7 * mm});
        }
        {
            var Q0;
            {var subQ0=sQuery(id+"F0.wireOp",EDGE,"E19");Q0=makeQuery(id+"F11.opExtrude","CAP_FACE",FACE,{"disambiguationData":[OSD([subQ0]),TDD([makeQuery(id+"F10.opChamfer","BLEND_FACE",FACE,{"disambiguationData":[OSD([subQ0]),TDD([makeQuery(id+"F3.opExtrude","CAP_EDGE",EDGE,{"disambiguationData":[OSD([subQ0]),TDD([makeQuery(id+"F0.imprint","IMPRINT",EDGE,{"disambiguationData":[TD([[makeQuery(id+"F0.imprint","INTERSECT",VERTEX,{"derivedFrom":[sQuery(id+"F0.wireOp",EDGE,"E18.bottom"),subQ0]}),1.0]])],"derivedFrom":subQ0})])],"isStart":false})])]})])],"isStart":false});}
            var Q1;
            {var subQ0=sQuery(id+"F0.wireOp",EDGE,"E19");Q1=makeQuery(id+"F11.opExtrude","CAP_FACE",FACE,{"disambiguationData":[OSD([subQ0]),TDD([makeQuery(id+"F10.opChamfer","BLEND_FACE",FACE,{"disambiguationData":[OSD([subQ0]),TDD([makeQuery(id+"F3.opExtrude","CAP_EDGE",EDGE,{"disambiguationData":[OSD([subQ0]),TDD([makeQuery(id+"F0.imprint","IMPRINT",EDGE,{"disambiguationData":[TD([[makeQuery(id+"F0.imprint","INTERSECT",VERTEX,{"derivedFrom":[subQ0,sQuery(id+"F0.wireOp",EDGE,"E24")]}),-1.0]])],"derivedFrom":subQ0})])],"isStart":false})])]})])],"isStart":false});}
            var Q2;
            {var subQ0=sQuery(id+"F0.wireOp",EDGE,"E19");Q2=makeQuery(id+"F11.opExtrude","CAP_FACE",FACE,{"disambiguationData":[OSD([subQ0]),TDD([makeQuery(id+"F10.opChamfer","BLEND_FACE",FACE,{"disambiguationData":[OSD([subQ0]),TDD([makeQuery(id+"F3.opExtrude","CAP_EDGE",EDGE,{"disambiguationData":[OSD([subQ0]),TDD([makeQuery(id+"F0.imprint","IMPRINT",EDGE,{"disambiguationData":[TD([[makeQuery(id+"F0.imprint","INTERSECT",VERTEX,{"derivedFrom":[subQ0,sQuery(id+"F0.wireOp",EDGE,"E28")]}),-1.0]])],"derivedFrom":subQ0})])],"isStart":false})])]})])],"isStart":false});}
            var Q3;
            {var subQ0=sQuery(id+"F0.wireOp",EDGE,"E19");Q3=makeQuery(id+"F11.opExtrude","CAP_FACE",FACE,{"disambiguationData":[OSD([subQ0]),TDD([makeQuery(id+"F10.opChamfer","BLEND_FACE",FACE,{"disambiguationData":[OSD([subQ0]),TDD([makeQuery(id+"F3.opExtrude","CAP_EDGE",EDGE,{"disambiguationData":[OSD([subQ0]),TDD([makeQuery(id+"F0.imprint","IMPRINT",EDGE,{"disambiguationData":[TD([[makeQuery(id+"F0.imprint","INTERSECT",VERTEX,{"derivedFrom":[sQuery(id+"F0.wireOp",EDGE,"E18.top"),subQ0]}),-1.0]])],"derivedFrom":subQ0})])],"isStart":false})])]})])],"isStart":false});}
            extrude(context, id + "F12", {"entities" : qUnion([Q0, Q1, Q2, Q3]), "operationType" : NewBodyOperationType.ADD, "depth" : 4 * mm});
        }
        {
            var Q0;
            Q0=makeQuery(id+"F12.opExtrude","CAP_EDGE",EDGE,{"disambiguationData":[OSD([sQuery(id+"F0.wireOp",EDGE,"E19"),sQuery(id+"F5.wireOp",EDGE,"E46.top")])],"isStart":false});
            chamfer(context, id + "F13", {"entities" : qUnion([Q0]), "chamferType" : ChamferType.TWO_OFFSETS, "width1" : 11.5 * mm, "oppositeDirection" : false, "width2" : 5 * mm, "tangentPropagation" : true});
        }
        {
            var Q0;
            {var subQ0=sQuery(id+"F0.wireOp",EDGE,"E20");Q0=makeQuery(id+"F3.opExtrude","CAP_EDGE",EDGE,{"disambiguationData":[OSD([subQ0]),TDD([makeQuery(id+"F0.imprint","IMPRINT",EDGE,{"disambiguationData":[TD([[makeQuery(id+"F0.imprint","INTERSECT",VERTEX,{"derivedFrom":[subQ0,sQuery(id+"F0.wireOp",EDGE,"E24")]}),-1.0]])],"derivedFrom":subQ0})])],"isStart":false});}
            var Q1;
            Q1=makeQuery(id+"F2.opExtrude","CAP_EDGE",EDGE,{"disambiguationData":[OSD([sQuery(id+"F0.wireOp",EDGE,"E21")])],"isStart":false});
            var Q2;
            {var subQ0=sQuery(id+"F0.wireOp",EDGE,"E20");Q2=makeQuery(id+"F3.opExtrude","CAP_EDGE",EDGE,{"disambiguationData":[OSD([subQ0]),TDD([makeQuery(id+"F0.imprint","IMPRINT",EDGE,{"disambiguationData":[TD([[makeQuery(id+"F0.imprint","INTERSECT",VERTEX,{"derivedFrom":[subQ0,sQuery(id+"F0.wireOp",EDGE,"E28")]}),-1.0]])],"derivedFrom":subQ0})])],"isStart":false});}
            var Q3;
            {var subQ0=sQuery(id+"F0.wireOp",EDGE,"E20");Q3=makeQuery(id+"F3.opExtrude","CAP_EDGE",EDGE,{"disambiguationData":[OSD([subQ0]),TDD([makeQuery(id+"F0.imprint","IMPRINT",EDGE,{"disambiguationData":[TD([[makeQuery(id+"F0.imprint","INTERSECT",VERTEX,{"derivedFrom":[sQuery(id+"F0.wireOp",EDGE,"E18.top"),subQ0]}),-1.0]])],"derivedFrom":subQ0})])],"isStart":false});}
            var Q4;
            {var subQ0=sQuery(id+"F0.wireOp",EDGE,"E20");Q4=makeQuery(id+"F3.opExtrude","CAP_EDGE",EDGE,{"disambiguationData":[OSD([subQ0]),TDD([makeQuery(id+"F0.imprint","IMPRINT",EDGE,{"disambiguationData":[TD([[makeQuery(id+"F0.imprint","INTERSECT",VERTEX,{"derivedFrom":[sQuery(id+"F0.wireOp",EDGE,"E18.bottom"),subQ0]}),1.0]])],"derivedFrom":subQ0})])],"isStart":false});}
            fillet(context, id + "F14", {"entities" : qUnion([Q0, Q1, Q2, Q3, Q4]), "radius" : 6 * mm, "allowEdgeOverflow" : false});
        }
        {
            var Q0;
            {var subQ0=sQuery(id+"F0.wireOp",EDGE,"E27");var subQ1=sQuery(id+"F0.wireOp",EDGE,"E20");var subQ2=sQuery(id+"F0.wireOp",EDGE,"E19");var subQ3=sQuery(id+"F0.wireOp",EDGE,"E18.bottom");Q0=makeQuery(id+"F12.boolean.opBoolean","MERGE",FACE,{"derivedFrom":[makeQuery(id+"F11.opExtrude","SWEPT_FACE",FACE,{"disambiguationData":[OSD([subQ3,subQ2,subQ1,subQ0])]}),makeQuery(id+"F12.opExtrude","SWEPT_FACE",FACE,{"disambiguationData":[OSD([subQ3,subQ2,subQ1,subQ0])]})]});}
            var Q1;
            {var subQ0=sQuery(id+"F0.wireOp",EDGE,"E25");var subQ1=sQuery(id+"F0.wireOp",EDGE,"E24");var subQ2=sQuery(id+"F0.wireOp",EDGE,"E20");var subQ3=sQuery(id+"F0.wireOp",EDGE,"E19");Q1=makeQuery(id+"F12.boolean.opBoolean","MERGE",FACE,{"derivedFrom":[makeQuery(id+"F11.opExtrude","SWEPT_FACE",FACE,{"disambiguationData":[OSD([subQ3,subQ2,subQ1,subQ0])]}),makeQuery(id+"F12.opExtrude","SWEPT_FACE",FACE,{"disambiguationData":[OSD([subQ3,subQ2,subQ1,subQ0])]})]});}
            var Q2;
            {var subQ0=sQuery(id+"F0.wireOp",EDGE,"E28");var subQ1=sQuery(id+"F0.wireOp",EDGE,"E22");var subQ2=sQuery(id+"F0.wireOp",EDGE,"E20");var subQ3=sQuery(id+"F0.wireOp",EDGE,"E19");Q2=makeQuery(id+"F12.boolean.opBoolean","MERGE",FACE,{"derivedFrom":[makeQuery(id+"F11.opExtrude","SWEPT_FACE",FACE,{"disambiguationData":[OSD([subQ3,subQ2,subQ1,subQ0])]}),makeQuery(id+"F12.opExtrude","SWEPT_FACE",FACE,{"disambiguationData":[OSD([subQ3,subQ2,subQ1,subQ0])]})]});}
            var Q3;
            {var subQ0=sQuery(id+"F0.wireOp",EDGE,"E30");var subQ1=sQuery(id+"F0.wireOp",EDGE,"E20");var subQ2=sQuery(id+"F0.wireOp",EDGE,"E19");var subQ3=sQuery(id+"F0.wireOp",EDGE,"E18.top");Q3=makeQuery(id+"F12.boolean.opBoolean","MERGE",FACE,{"derivedFrom":[makeQuery(id+"F11.opExtrude","SWEPT_FACE",FACE,{"disambiguationData":[OSD([subQ3,subQ2,subQ1,subQ0])]}),makeQuery(id+"F12.opExtrude","SWEPT_FACE",FACE,{"disambiguationData":[OSD([subQ3,subQ2,subQ1,subQ0])]})]});}
            extrude(context, id + "F15", {"entities" : qUnion([Q0, Q1, Q2, Q3]), "operationType" : NewBodyOperationType.ADD, "depth" : 2 * mm});
        }
        {
            var Q0;
            {var subQ0=sQuery(id+"F0.wireOp",EDGE,"E19");var subQ1=sQuery(id+"F0.wireOp",EDGE,"E18.right");var subQ2=sQuery(id+"F0.wireOp",EDGE,"E18.top");var subQ3=sQuery(id+"F0.wireOp",EDGE,"E18.bottom");var subQ4=sQuery(id+"F0.wireOp",EDGE,"E25");var subQ5=sQuery(id+"F0.wireOp",EDGE,"E24");var subQ6=sQuery(id+"F0.wireOp",EDGE,"E20");var subQ7=sQuery(id+"F0.wireOp",EDGE,"E28");var subQ8=sQuery(id+"F0.wireOp",EDGE,"E22");var subQ9=sQuery(id+"F0.wireOp",EDGE,"E30");var subQ10=sQuery(id+"F0.wireOp",EDGE,"E27");var subQ11=sQuery(id+"F0.wireOp",EDGE,"E21");Q0=makeQuery(id+"F9.opChamfer","BLEND_EDGE",EDGE,{"disambiguationData":[OD(2.0)],"blendedFrom":[makeQuery(id+"F4.opExtrude","CAP_EDGE",EDGE,{"disambiguationData":[OSD([subQ1])],"isStart":true}),makeQuery(id+"F4.boolean.opBoolean","MERGE",FACE,{"derivedFrom":[makeQuery(id+"F3.boolean.opBoolean","MERGE",FACE,{"derivedFrom":[makeQuery(id+"F2.boolean.opBoolean","MERGE",FACE,{"derivedFrom":[makeQuery(id+"F1.opExtrude","CAP_FACE",FACE,{"disambiguationData":[OSD([sQuery(id+"F0.wireOp",EDGE,"E14"),sQuery(id+"F0.wireOp",EDGE,"E15"),sQuery(id+"F0.wireOp",EDGE,"E16"),sQuery(id+"F0.wireOp",EDGE,"E17"),subQ3,subQ2,sQuery(id+"F0.wireOp",EDGE,"E18.left"),subQ11,sQuery(id+"F0.wireOp",EDGE,"E32"),sQuery(id+"F0.wireOp",EDGE,"udVUNbQT-3sfe-87Jq-HJqa-fJdtHQiA1hvh"),sQuery(id+"F0.wireOp",EDGE,"JFR9UDWr-vphY-3fZN-ekGv-NYTzQ2OyldDi"),sQuery(id+"F0.wireOp",EDGE,"E33"),sQuery(id+"F0.wireOp",EDGE,"E34.bottom"),sQuery(id+"F0.wireOp",EDGE,"E34.top"),sQuery(id+"F0.wireOp",EDGE,"E34.left"),sQuery(id+"F0.wireOp",EDGE,"E34.right"),sQuery(id+"F0.wireOp",EDGE,"E35.bottom"),sQuery(id+"F0.wireOp",EDGE,"E35.top"),sQuery(id+"F0.wireOp",EDGE,"E35.left"),sQuery(id+"F0.wireOp",EDGE,"E35.right"),sQuery(id+"F0.wireOp",EDGE,"dDL4M1PI-aelY-u7zt-lnq0-sMzwrNtlq2yo"),sQuery(id+"F0.wireOp",EDGE,"E36")])],"isStart":true}),makeQuery(id+"F2.opExtrude","CAP_FACE",FACE,{"disambiguationData":[OSD([subQ3,subQ2,subQ6,subQ11,subQ8,sQuery(id+"F0.wireOp",EDGE,"E23"),subQ5,subQ4,sQuery(id+"F0.wireOp",EDGE,"E26"),subQ10,subQ7,sQuery(id+"F0.wireOp",EDGE,"E29"),subQ9])],"isStart":true})]}),makeQuery(id+"F3.opExtrude","CAP_FACE",FACE,{"disambiguationData":[OSD([subQ3,subQ0,subQ6,subQ10])],"isStart":true}),makeQuery(id+"F3.opExtrude","CAP_FACE",FACE,{"disambiguationData":[OSD([subQ2,subQ0,subQ6,subQ9])],"isStart":true}),makeQuery(id+"F3.opExtrude","CAP_FACE",FACE,{"disambiguationData":[OSD([subQ0,subQ6,subQ8,subQ7])],"isStart":true}),makeQuery(id+"F3.opExtrude","CAP_FACE",FACE,{"disambiguationData":[OSD([subQ0,subQ6,subQ5,subQ4])],"isStart":true})]}),makeQuery(id+"F4.opExtrude","CAP_FACE",FACE,{"disambiguationData":[OSD([subQ3,subQ2,subQ1,subQ0])],"isStart":true})]})],"blendedInto":[makeQuery(id+"F4.boolean.opBoolean","MERGE",FACE,{"derivedFrom":[makeQuery(id+"F3.boolean.opBoolean","MERGE",FACE,{"derivedFrom":[makeQuery(id+"F2.boolean.opBoolean","MERGE",FACE,{"derivedFrom":[makeQuery(id+"F1.opExtrude","CAP_FACE",FACE,{"disambiguationData":[OSD([sQuery(id+"F0.wireOp",EDGE,"E14"),sQuery(id+"F0.wireOp",EDGE,"E15"),sQuery(id+"F0.wireOp",EDGE,"E16"),sQuery(id+"F0.wireOp",EDGE,"E17"),subQ3,subQ2,sQuery(id+"F0.wireOp",EDGE,"E18.left"),subQ11,sQuery(id+"F0.wireOp",EDGE,"E32"),sQuery(id+"F0.wireOp",EDGE,"udVUNbQT-3sfe-87Jq-HJqa-fJdtHQiA1hvh"),sQuery(id+"F0.wireOp",EDGE,"JFR9UDWr-vphY-3fZN-ekGv-NYTzQ2OyldDi"),sQuery(id+"F0.wireOp",EDGE,"E33"),sQuery(id+"F0.wireOp",EDGE,"E34.bottom"),sQuery(id+"F0.wireOp",EDGE,"E34.top"),sQuery(id+"F0.wireOp",EDGE,"E34.left"),sQuery(id+"F0.wireOp",EDGE,"E34.right"),sQuery(id+"F0.wireOp",EDGE,"E35.bottom"),sQuery(id+"F0.wireOp",EDGE,"E35.top"),sQuery(id+"F0.wireOp",EDGE,"E35.left"),sQuery(id+"F0.wireOp",EDGE,"E35.right"),sQuery(id+"F0.wireOp",EDGE,"dDL4M1PI-aelY-u7zt-lnq0-sMzwrNtlq2yo"),sQuery(id+"F0.wireOp",EDGE,"E36")])],"isStart":true}),makeQuery(id+"F2.opExtrude","CAP_FACE",FACE,{"disambiguationData":[OSD([subQ3,subQ2,subQ6,subQ11,subQ8,sQuery(id+"F0.wireOp",EDGE,"E23"),subQ5,subQ4,sQuery(id+"F0.wireOp",EDGE,"E26"),subQ10,subQ7,sQuery(id+"F0.wireOp",EDGE,"E29"),subQ9])],"isStart":true})]}),makeQuery(id+"F3.opExtrude","CAP_FACE",FACE,{"disambiguationData":[OSD([subQ3,subQ0,subQ6,subQ10])],"isStart":true}),makeQuery(id+"F3.opExtrude","CAP_FACE",FACE,{"disambiguationData":[OSD([subQ2,subQ0,subQ6,subQ9])],"isStart":true}),makeQuery(id+"F3.opExtrude","CAP_FACE",FACE,{"disambiguationData":[OSD([subQ0,subQ6,subQ8,subQ7])],"isStart":true}),makeQuery(id+"F3.opExtrude","CAP_FACE",FACE,{"disambiguationData":[OSD([subQ0,subQ6,subQ5,subQ4])],"isStart":true})]}),makeQuery(id+"F4.opExtrude","CAP_FACE",FACE,{"disambiguationData":[OSD([subQ3,subQ2,subQ1,subQ0])],"isStart":true})]})]});}
            var Q1;
            {var subQ0=sQuery(id+"F0.wireOp",EDGE,"E19");var subQ1=sQuery(id+"F0.wireOp",EDGE,"E18.right");var subQ2=sQuery(id+"F0.wireOp",EDGE,"E18.top");var subQ3=sQuery(id+"F0.wireOp",EDGE,"E18.bottom");var subQ4=sQuery(id+"F0.wireOp",EDGE,"E25");var subQ5=sQuery(id+"F0.wireOp",EDGE,"E24");var subQ6=sQuery(id+"F0.wireOp",EDGE,"E20");var subQ7=sQuery(id+"F0.wireOp",EDGE,"E28");var subQ8=sQuery(id+"F0.wireOp",EDGE,"E22");var subQ9=sQuery(id+"F0.wireOp",EDGE,"E30");var subQ10=sQuery(id+"F0.wireOp",EDGE,"E27");var subQ11=sQuery(id+"F0.wireOp",EDGE,"E21");Q1=makeQuery(id+"F9.opChamfer","BLEND_EDGE",EDGE,{"disambiguationData":[OD(1.0)],"blendedFrom":[makeQuery(id+"F4.opExtrude","CAP_EDGE",EDGE,{"disambiguationData":[OSD([subQ1])],"isStart":true}),makeQuery(id+"F4.boolean.opBoolean","MERGE",FACE,{"derivedFrom":[makeQuery(id+"F3.boolean.opBoolean","MERGE",FACE,{"derivedFrom":[makeQuery(id+"F2.boolean.opBoolean","MERGE",FACE,{"derivedFrom":[makeQuery(id+"F1.opExtrude","CAP_FACE",FACE,{"disambiguationData":[OSD([sQuery(id+"F0.wireOp",EDGE,"E14"),sQuery(id+"F0.wireOp",EDGE,"E15"),sQuery(id+"F0.wireOp",EDGE,"E16"),sQuery(id+"F0.wireOp",EDGE,"E17"),subQ3,subQ2,sQuery(id+"F0.wireOp",EDGE,"E18.left"),subQ11,sQuery(id+"F0.wireOp",EDGE,"E32"),sQuery(id+"F0.wireOp",EDGE,"udVUNbQT-3sfe-87Jq-HJqa-fJdtHQiA1hvh"),sQuery(id+"F0.wireOp",EDGE,"JFR9UDWr-vphY-3fZN-ekGv-NYTzQ2OyldDi"),sQuery(id+"F0.wireOp",EDGE,"E33"),sQuery(id+"F0.wireOp",EDGE,"E34.bottom"),sQuery(id+"F0.wireOp",EDGE,"E34.top"),sQuery(id+"F0.wireOp",EDGE,"E34.left"),sQuery(id+"F0.wireOp",EDGE,"E34.right"),sQuery(id+"F0.wireOp",EDGE,"E35.bottom"),sQuery(id+"F0.wireOp",EDGE,"E35.top"),sQuery(id+"F0.wireOp",EDGE,"E35.left"),sQuery(id+"F0.wireOp",EDGE,"E35.right"),sQuery(id+"F0.wireOp",EDGE,"dDL4M1PI-aelY-u7zt-lnq0-sMzwrNtlq2yo"),sQuery(id+"F0.wireOp",EDGE,"E36")])],"isStart":true}),makeQuery(id+"F2.opExtrude","CAP_FACE",FACE,{"disambiguationData":[OSD([subQ3,subQ2,subQ6,subQ11,subQ8,sQuery(id+"F0.wireOp",EDGE,"E23"),subQ5,subQ4,sQuery(id+"F0.wireOp",EDGE,"E26"),subQ10,subQ7,sQuery(id+"F0.wireOp",EDGE,"E29"),subQ9])],"isStart":true})]}),makeQuery(id+"F3.opExtrude","CAP_FACE",FACE,{"disambiguationData":[OSD([subQ3,subQ0,subQ6,subQ10])],"isStart":true}),makeQuery(id+"F3.opExtrude","CAP_FACE",FACE,{"disambiguationData":[OSD([subQ2,subQ0,subQ6,subQ9])],"isStart":true}),makeQuery(id+"F3.opExtrude","CAP_FACE",FACE,{"disambiguationData":[OSD([subQ0,subQ6,subQ8,subQ7])],"isStart":true}),makeQuery(id+"F3.opExtrude","CAP_FACE",FACE,{"disambiguationData":[OSD([subQ0,subQ6,subQ5,subQ4])],"isStart":true})]}),makeQuery(id+"F4.opExtrude","CAP_FACE",FACE,{"disambiguationData":[OSD([subQ3,subQ2,subQ1,subQ0])],"isStart":true})]})],"blendedInto":[makeQuery(id+"F4.boolean.opBoolean","MERGE",FACE,{"derivedFrom":[makeQuery(id+"F3.boolean.opBoolean","MERGE",FACE,{"derivedFrom":[makeQuery(id+"F2.boolean.opBoolean","MERGE",FACE,{"derivedFrom":[makeQuery(id+"F1.opExtrude","CAP_FACE",FACE,{"disambiguationData":[OSD([sQuery(id+"F0.wireOp",EDGE,"E14"),sQuery(id+"F0.wireOp",EDGE,"E15"),sQuery(id+"F0.wireOp",EDGE,"E16"),sQuery(id+"F0.wireOp",EDGE,"E17"),subQ3,subQ2,sQuery(id+"F0.wireOp",EDGE,"E18.left"),subQ11,sQuery(id+"F0.wireOp",EDGE,"E32"),sQuery(id+"F0.wireOp",EDGE,"udVUNbQT-3sfe-87Jq-HJqa-fJdtHQiA1hvh"),sQuery(id+"F0.wireOp",EDGE,"JFR9UDWr-vphY-3fZN-ekGv-NYTzQ2OyldDi"),sQuery(id+"F0.wireOp",EDGE,"E33"),sQuery(id+"F0.wireOp",EDGE,"E34.bottom"),sQuery(id+"F0.wireOp",EDGE,"E34.top"),sQuery(id+"F0.wireOp",EDGE,"E34.left"),sQuery(id+"F0.wireOp",EDGE,"E34.right"),sQuery(id+"F0.wireOp",EDGE,"E35.bottom"),sQuery(id+"F0.wireOp",EDGE,"E35.top"),sQuery(id+"F0.wireOp",EDGE,"E35.left"),sQuery(id+"F0.wireOp",EDGE,"E35.right"),sQuery(id+"F0.wireOp",EDGE,"dDL4M1PI-aelY-u7zt-lnq0-sMzwrNtlq2yo"),sQuery(id+"F0.wireOp",EDGE,"E36")])],"isStart":true}),makeQuery(id+"F2.opExtrude","CAP_FACE",FACE,{"disambiguationData":[OSD([subQ3,subQ2,subQ6,subQ11,subQ8,sQuery(id+"F0.wireOp",EDGE,"E23"),subQ5,subQ4,sQuery(id+"F0.wireOp",EDGE,"E26"),subQ10,subQ7,sQuery(id+"F0.wireOp",EDGE,"E29"),subQ9])],"isStart":true})]}),makeQuery(id+"F3.opExtrude","CAP_FACE",FACE,{"disambiguationData":[OSD([subQ3,subQ0,subQ6,subQ10])],"isStart":true}),makeQuery(id+"F3.opExtrude","CAP_FACE",FACE,{"disambiguationData":[OSD([subQ2,subQ0,subQ6,subQ9])],"isStart":true}),makeQuery(id+"F3.opExtrude","CAP_FACE",FACE,{"disambiguationData":[OSD([subQ0,subQ6,subQ8,subQ7])],"isStart":true}),makeQuery(id+"F3.opExtrude","CAP_FACE",FACE,{"disambiguationData":[OSD([subQ0,subQ6,subQ5,subQ4])],"isStart":true})]}),makeQuery(id+"F4.opExtrude","CAP_FACE",FACE,{"disambiguationData":[OSD([subQ3,subQ2,subQ1,subQ0])],"isStart":true})]})]});}
            var Q2;
            {var subQ0=sQuery(id+"F0.wireOp",EDGE,"E19");var subQ1=sQuery(id+"F0.wireOp",EDGE,"E18.right");var subQ2=sQuery(id+"F0.wireOp",EDGE,"E18.top");var subQ3=sQuery(id+"F0.wireOp",EDGE,"E18.bottom");var subQ4=sQuery(id+"F0.wireOp",EDGE,"E25");var subQ5=sQuery(id+"F0.wireOp",EDGE,"E24");var subQ6=sQuery(id+"F0.wireOp",EDGE,"E20");var subQ7=sQuery(id+"F0.wireOp",EDGE,"E28");var subQ8=sQuery(id+"F0.wireOp",EDGE,"E22");var subQ9=sQuery(id+"F0.wireOp",EDGE,"E30");var subQ10=sQuery(id+"F0.wireOp",EDGE,"E27");var subQ11=sQuery(id+"F0.wireOp",EDGE,"E21");Q2=makeQuery(id+"F9.opChamfer","BLEND_EDGE",EDGE,{"disambiguationData":[OD(0.0)],"blendedFrom":[makeQuery(id+"F4.opExtrude","CAP_EDGE",EDGE,{"disambiguationData":[OSD([subQ1])],"isStart":true}),makeQuery(id+"F4.boolean.opBoolean","MERGE",FACE,{"derivedFrom":[makeQuery(id+"F3.boolean.opBoolean","MERGE",FACE,{"derivedFrom":[makeQuery(id+"F2.boolean.opBoolean","MERGE",FACE,{"derivedFrom":[makeQuery(id+"F1.opExtrude","CAP_FACE",FACE,{"disambiguationData":[OSD([sQuery(id+"F0.wireOp",EDGE,"E14"),sQuery(id+"F0.wireOp",EDGE,"E15"),sQuery(id+"F0.wireOp",EDGE,"E16"),sQuery(id+"F0.wireOp",EDGE,"E17"),subQ3,subQ2,sQuery(id+"F0.wireOp",EDGE,"E18.left"),subQ11,sQuery(id+"F0.wireOp",EDGE,"E32"),sQuery(id+"F0.wireOp",EDGE,"udVUNbQT-3sfe-87Jq-HJqa-fJdtHQiA1hvh"),sQuery(id+"F0.wireOp",EDGE,"JFR9UDWr-vphY-3fZN-ekGv-NYTzQ2OyldDi"),sQuery(id+"F0.wireOp",EDGE,"E33"),sQuery(id+"F0.wireOp",EDGE,"E34.bottom"),sQuery(id+"F0.wireOp",EDGE,"E34.top"),sQuery(id+"F0.wireOp",EDGE,"E34.left"),sQuery(id+"F0.wireOp",EDGE,"E34.right"),sQuery(id+"F0.wireOp",EDGE,"E35.bottom"),sQuery(id+"F0.wireOp",EDGE,"E35.top"),sQuery(id+"F0.wireOp",EDGE,"E35.left"),sQuery(id+"F0.wireOp",EDGE,"E35.right"),sQuery(id+"F0.wireOp",EDGE,"dDL4M1PI-aelY-u7zt-lnq0-sMzwrNtlq2yo"),sQuery(id+"F0.wireOp",EDGE,"E36")])],"isStart":true}),makeQuery(id+"F2.opExtrude","CAP_FACE",FACE,{"disambiguationData":[OSD([subQ3,subQ2,subQ6,subQ11,subQ8,sQuery(id+"F0.wireOp",EDGE,"E23"),subQ5,subQ4,sQuery(id+"F0.wireOp",EDGE,"E26"),subQ10,subQ7,sQuery(id+"F0.wireOp",EDGE,"E29"),subQ9])],"isStart":true})]}),makeQuery(id+"F3.opExtrude","CAP_FACE",FACE,{"disambiguationData":[OSD([subQ3,subQ0,subQ6,subQ10])],"isStart":true}),makeQuery(id+"F3.opExtrude","CAP_FACE",FACE,{"disambiguationData":[OSD([subQ2,subQ0,subQ6,subQ9])],"isStart":true}),makeQuery(id+"F3.opExtrude","CAP_FACE",FACE,{"disambiguationData":[OSD([subQ0,subQ6,subQ8,subQ7])],"isStart":true}),makeQuery(id+"F3.opExtrude","CAP_FACE",FACE,{"disambiguationData":[OSD([subQ0,subQ6,subQ5,subQ4])],"isStart":true})]}),makeQuery(id+"F4.opExtrude","CAP_FACE",FACE,{"disambiguationData":[OSD([subQ3,subQ2,subQ1,subQ0])],"isStart":true})]})],"blendedInto":[makeQuery(id+"F4.boolean.opBoolean","MERGE",FACE,{"derivedFrom":[makeQuery(id+"F3.boolean.opBoolean","MERGE",FACE,{"derivedFrom":[makeQuery(id+"F2.boolean.opBoolean","MERGE",FACE,{"derivedFrom":[makeQuery(id+"F1.opExtrude","CAP_FACE",FACE,{"disambiguationData":[OSD([sQuery(id+"F0.wireOp",EDGE,"E14"),sQuery(id+"F0.wireOp",EDGE,"E15"),sQuery(id+"F0.wireOp",EDGE,"E16"),sQuery(id+"F0.wireOp",EDGE,"E17"),subQ3,subQ2,sQuery(id+"F0.wireOp",EDGE,"E18.left"),subQ11,sQuery(id+"F0.wireOp",EDGE,"E32"),sQuery(id+"F0.wireOp",EDGE,"udVUNbQT-3sfe-87Jq-HJqa-fJdtHQiA1hvh"),sQuery(id+"F0.wireOp",EDGE,"JFR9UDWr-vphY-3fZN-ekGv-NYTzQ2OyldDi"),sQuery(id+"F0.wireOp",EDGE,"E33"),sQuery(id+"F0.wireOp",EDGE,"E34.bottom"),sQuery(id+"F0.wireOp",EDGE,"E34.top"),sQuery(id+"F0.wireOp",EDGE,"E34.left"),sQuery(id+"F0.wireOp",EDGE,"E34.right"),sQuery(id+"F0.wireOp",EDGE,"E35.bottom"),sQuery(id+"F0.wireOp",EDGE,"E35.top"),sQuery(id+"F0.wireOp",EDGE,"E35.left"),sQuery(id+"F0.wireOp",EDGE,"E35.right"),sQuery(id+"F0.wireOp",EDGE,"dDL4M1PI-aelY-u7zt-lnq0-sMzwrNtlq2yo"),sQuery(id+"F0.wireOp",EDGE,"E36")])],"isStart":true}),makeQuery(id+"F2.opExtrude","CAP_FACE",FACE,{"disambiguationData":[OSD([subQ3,subQ2,subQ6,subQ11,subQ8,sQuery(id+"F0.wireOp",EDGE,"E23"),subQ5,subQ4,sQuery(id+"F0.wireOp",EDGE,"E26"),subQ10,subQ7,sQuery(id+"F0.wireOp",EDGE,"E29"),subQ9])],"isStart":true})]}),makeQuery(id+"F3.opExtrude","CAP_FACE",FACE,{"disambiguationData":[OSD([subQ3,subQ0,subQ6,subQ10])],"isStart":true}),makeQuery(id+"F3.opExtrude","CAP_FACE",FACE,{"disambiguationData":[OSD([subQ2,subQ0,subQ6,subQ9])],"isStart":true}),makeQuery(id+"F3.opExtrude","CAP_FACE",FACE,{"disambiguationData":[OSD([subQ0,subQ6,subQ8,subQ7])],"isStart":true}),makeQuery(id+"F3.opExtrude","CAP_FACE",FACE,{"disambiguationData":[OSD([subQ0,subQ6,subQ5,subQ4])],"isStart":true})]}),makeQuery(id+"F4.opExtrude","CAP_FACE",FACE,{"disambiguationData":[OSD([subQ3,subQ2,subQ1,subQ0])],"isStart":true})]})]});}
            var Q3;
            {var subQ0=sQuery(id+"F0.wireOp",EDGE,"E19");var subQ1=sQuery(id+"F0.wireOp",EDGE,"E18.right");var subQ2=sQuery(id+"F0.wireOp",EDGE,"E18.top");var subQ3=sQuery(id+"F0.wireOp",EDGE,"E18.bottom");var subQ4=sQuery(id+"F0.wireOp",EDGE,"E25");var subQ5=sQuery(id+"F0.wireOp",EDGE,"E24");var subQ6=sQuery(id+"F0.wireOp",EDGE,"E20");var subQ7=sQuery(id+"F0.wireOp",EDGE,"E28");var subQ8=sQuery(id+"F0.wireOp",EDGE,"E22");var subQ9=sQuery(id+"F0.wireOp",EDGE,"E30");var subQ10=sQuery(id+"F0.wireOp",EDGE,"E27");var subQ11=sQuery(id+"F0.wireOp",EDGE,"E21");Q3=makeQuery(id+"F9.opChamfer","BLEND_EDGE",EDGE,{"disambiguationData":[OD(3.0)],"blendedFrom":[makeQuery(id+"F4.opExtrude","CAP_EDGE",EDGE,{"disambiguationData":[OSD([subQ1])],"isStart":true}),makeQuery(id+"F4.boolean.opBoolean","MERGE",FACE,{"derivedFrom":[makeQuery(id+"F3.boolean.opBoolean","MERGE",FACE,{"derivedFrom":[makeQuery(id+"F2.boolean.opBoolean","MERGE",FACE,{"derivedFrom":[makeQuery(id+"F1.opExtrude","CAP_FACE",FACE,{"disambiguationData":[OSD([sQuery(id+"F0.wireOp",EDGE,"E14"),sQuery(id+"F0.wireOp",EDGE,"E15"),sQuery(id+"F0.wireOp",EDGE,"E16"),sQuery(id+"F0.wireOp",EDGE,"E17"),subQ3,subQ2,sQuery(id+"F0.wireOp",EDGE,"E18.left"),subQ11,sQuery(id+"F0.wireOp",EDGE,"E32"),sQuery(id+"F0.wireOp",EDGE,"udVUNbQT-3sfe-87Jq-HJqa-fJdtHQiA1hvh"),sQuery(id+"F0.wireOp",EDGE,"JFR9UDWr-vphY-3fZN-ekGv-NYTzQ2OyldDi"),sQuery(id+"F0.wireOp",EDGE,"E33"),sQuery(id+"F0.wireOp",EDGE,"E34.bottom"),sQuery(id+"F0.wireOp",EDGE,"E34.top"),sQuery(id+"F0.wireOp",EDGE,"E34.left"),sQuery(id+"F0.wireOp",EDGE,"E34.right"),sQuery(id+"F0.wireOp",EDGE,"E35.bottom"),sQuery(id+"F0.wireOp",EDGE,"E35.top"),sQuery(id+"F0.wireOp",EDGE,"E35.left"),sQuery(id+"F0.wireOp",EDGE,"E35.right"),sQuery(id+"F0.wireOp",EDGE,"dDL4M1PI-aelY-u7zt-lnq0-sMzwrNtlq2yo"),sQuery(id+"F0.wireOp",EDGE,"E36")])],"isStart":true}),makeQuery(id+"F2.opExtrude","CAP_FACE",FACE,{"disambiguationData":[OSD([subQ3,subQ2,subQ6,subQ11,subQ8,sQuery(id+"F0.wireOp",EDGE,"E23"),subQ5,subQ4,sQuery(id+"F0.wireOp",EDGE,"E26"),subQ10,subQ7,sQuery(id+"F0.wireOp",EDGE,"E29"),subQ9])],"isStart":true})]}),makeQuery(id+"F3.opExtrude","CAP_FACE",FACE,{"disambiguationData":[OSD([subQ3,subQ0,subQ6,subQ10])],"isStart":true}),makeQuery(id+"F3.opExtrude","CAP_FACE",FACE,{"disambiguationData":[OSD([subQ2,subQ0,subQ6,subQ9])],"isStart":true}),makeQuery(id+"F3.opExtrude","CAP_FACE",FACE,{"disambiguationData":[OSD([subQ0,subQ6,subQ8,subQ7])],"isStart":true}),makeQuery(id+"F3.opExtrude","CAP_FACE",FACE,{"disambiguationData":[OSD([subQ0,subQ6,subQ5,subQ4])],"isStart":true})]}),makeQuery(id+"F4.opExtrude","CAP_FACE",FACE,{"disambiguationData":[OSD([subQ3,subQ2,subQ1,subQ0])],"isStart":true})]})],"blendedInto":[makeQuery(id+"F4.boolean.opBoolean","MERGE",FACE,{"derivedFrom":[makeQuery(id+"F3.boolean.opBoolean","MERGE",FACE,{"derivedFrom":[makeQuery(id+"F2.boolean.opBoolean","MERGE",FACE,{"derivedFrom":[makeQuery(id+"F1.opExtrude","CAP_FACE",FACE,{"disambiguationData":[OSD([sQuery(id+"F0.wireOp",EDGE,"E14"),sQuery(id+"F0.wireOp",EDGE,"E15"),sQuery(id+"F0.wireOp",EDGE,"E16"),sQuery(id+"F0.wireOp",EDGE,"E17"),subQ3,subQ2,sQuery(id+"F0.wireOp",EDGE,"E18.left"),subQ11,sQuery(id+"F0.wireOp",EDGE,"E32"),sQuery(id+"F0.wireOp",EDGE,"udVUNbQT-3sfe-87Jq-HJqa-fJdtHQiA1hvh"),sQuery(id+"F0.wireOp",EDGE,"JFR9UDWr-vphY-3fZN-ekGv-NYTzQ2OyldDi"),sQuery(id+"F0.wireOp",EDGE,"E33"),sQuery(id+"F0.wireOp",EDGE,"E34.bottom"),sQuery(id+"F0.wireOp",EDGE,"E34.top"),sQuery(id+"F0.wireOp",EDGE,"E34.left"),sQuery(id+"F0.wireOp",EDGE,"E34.right"),sQuery(id+"F0.wireOp",EDGE,"E35.bottom"),sQuery(id+"F0.wireOp",EDGE,"E35.top"),sQuery(id+"F0.wireOp",EDGE,"E35.left"),sQuery(id+"F0.wireOp",EDGE,"E35.right"),sQuery(id+"F0.wireOp",EDGE,"dDL4M1PI-aelY-u7zt-lnq0-sMzwrNtlq2yo"),sQuery(id+"F0.wireOp",EDGE,"E36")])],"isStart":true}),makeQuery(id+"F2.opExtrude","CAP_FACE",FACE,{"disambiguationData":[OSD([subQ3,subQ2,subQ6,subQ11,subQ8,sQuery(id+"F0.wireOp",EDGE,"E23"),subQ5,subQ4,sQuery(id+"F0.wireOp",EDGE,"E26"),subQ10,subQ7,sQuery(id+"F0.wireOp",EDGE,"E29"),subQ9])],"isStart":true})]}),makeQuery(id+"F3.opExtrude","CAP_FACE",FACE,{"disambiguationData":[OSD([subQ3,subQ0,subQ6,subQ10])],"isStart":true}),makeQuery(id+"F3.opExtrude","CAP_FACE",FACE,{"disambiguationData":[OSD([subQ2,subQ0,subQ6,subQ9])],"isStart":true}),makeQuery(id+"F3.opExtrude","CAP_FACE",FACE,{"disambiguationData":[OSD([subQ0,subQ6,subQ8,subQ7])],"isStart":true}),makeQuery(id+"F3.opExtrude","CAP_FACE",FACE,{"disambiguationData":[OSD([subQ0,subQ6,subQ5,subQ4])],"isStart":true})]}),makeQuery(id+"F4.opExtrude","CAP_FACE",FACE,{"disambiguationData":[OSD([subQ3,subQ2,subQ1,subQ0])],"isStart":true})]})]});}
            fillet(context, id + "F16", {"entities" : qUnion([Q0, Q1, Q2, Q3]), "radius" : 5 * mm, "tangentPropagation" : true, "allowEdgeOverflow" : false});
        }
        {
            var Q0;
            {var subQ0=sQuery(id+"F0.wireOp",EDGE,"E27");var subQ1=sQuery(id+"F0.wireOp",EDGE,"E20");var subQ2=sQuery(id+"F0.wireOp",EDGE,"E19");var subQ3=sQuery(id+"F0.wireOp",EDGE,"E18.bottom");Q0=makeQuery(id+"F15.opExtrude","CAP_EDGE",EDGE,{"disambiguationData":[OSD([subQ3,subQ2,subQ1,subQ0]),TDD([makeQuery(id+"F11.boolean.opBoolean","MERGE",EDGE,{"derivedFrom":[makeQuery(id+"F10.opChamfer","BLEND_EDGE",EDGE,{"blendedFrom":[makeQuery(id+"F3.opExtrude","CAP_EDGE",EDGE,{"disambiguationData":[OSD([subQ2]),TDD([makeQuery(id+"F0.imprint","IMPRINT",EDGE,{"disambiguationData":[TD([[makeQuery(id+"F0.imprint","INTERSECT",VERTEX,{"derivedFrom":[subQ3,subQ2]}),1.0]])],"derivedFrom":subQ2})])],"isStart":false}),makeQuery(id+"F3.opExtrude","CAP_FACE",FACE,{"disambiguationData":[OSD([subQ3,subQ2,subQ1,subQ0])],"isStart":false})],"blendedInto":[makeQuery(id+"F3.opExtrude","CAP_FACE",FACE,{"disambiguationData":[OSD([subQ3,subQ2,subQ1,subQ0])],"isStart":false})]}),makeQuery(id+"F11.opExtrude","CAP_EDGE",EDGE,{"disambiguationData":[OSD([subQ3,subQ2,subQ1,subQ0])],"isStart":true})]})])],"isStart":false});}
            var Q1;
            {var subQ0=sQuery(id+"F0.wireOp",EDGE,"E25");var subQ1=sQuery(id+"F0.wireOp",EDGE,"E24");var subQ2=sQuery(id+"F0.wireOp",EDGE,"E20");var subQ3=sQuery(id+"F0.wireOp",EDGE,"E19");Q1=makeQuery(id+"F15.opExtrude","CAP_EDGE",EDGE,{"disambiguationData":[OSD([subQ3,subQ2,subQ1,subQ0]),TDD([makeQuery(id+"F11.boolean.opBoolean","MERGE",EDGE,{"derivedFrom":[makeQuery(id+"F10.opChamfer","BLEND_EDGE",EDGE,{"blendedFrom":[makeQuery(id+"F3.opExtrude","CAP_EDGE",EDGE,{"disambiguationData":[OSD([subQ3]),TDD([makeQuery(id+"F0.imprint","IMPRINT",EDGE,{"disambiguationData":[TD([[makeQuery(id+"F0.imprint","INTERSECT",VERTEX,{"derivedFrom":[subQ3,subQ1]}),-1.0]])],"derivedFrom":subQ3})])],"isStart":false}),makeQuery(id+"F3.opExtrude","CAP_FACE",FACE,{"disambiguationData":[OSD([subQ3,subQ2,subQ1,subQ0])],"isStart":false})],"blendedInto":[makeQuery(id+"F3.opExtrude","CAP_FACE",FACE,{"disambiguationData":[OSD([subQ3,subQ2,subQ1,subQ0])],"isStart":false})]}),makeQuery(id+"F11.opExtrude","CAP_EDGE",EDGE,{"disambiguationData":[OSD([subQ3,subQ2,subQ1,subQ0])],"isStart":true})]})])],"isStart":false});}
            var Q2;
            {var subQ0=sQuery(id+"F0.wireOp",EDGE,"E28");var subQ1=sQuery(id+"F0.wireOp",EDGE,"E22");var subQ2=sQuery(id+"F0.wireOp",EDGE,"E20");var subQ3=sQuery(id+"F0.wireOp",EDGE,"E19");Q2=makeQuery(id+"F15.opExtrude","CAP_EDGE",EDGE,{"disambiguationData":[OSD([subQ3,subQ2,subQ1,subQ0]),TDD([makeQuery(id+"F11.boolean.opBoolean","MERGE",EDGE,{"derivedFrom":[makeQuery(id+"F10.opChamfer","BLEND_EDGE",EDGE,{"blendedFrom":[makeQuery(id+"F3.opExtrude","CAP_EDGE",EDGE,{"disambiguationData":[OSD([subQ3]),TDD([makeQuery(id+"F0.imprint","IMPRINT",EDGE,{"disambiguationData":[TD([[makeQuery(id+"F0.imprint","INTERSECT",VERTEX,{"derivedFrom":[subQ3,subQ0]}),-1.0]])],"derivedFrom":subQ3})])],"isStart":false}),makeQuery(id+"F3.opExtrude","CAP_FACE",FACE,{"disambiguationData":[OSD([subQ3,subQ2,subQ1,subQ0])],"isStart":false})],"blendedInto":[makeQuery(id+"F3.opExtrude","CAP_FACE",FACE,{"disambiguationData":[OSD([subQ3,subQ2,subQ1,subQ0])],"isStart":false})]}),makeQuery(id+"F11.opExtrude","CAP_EDGE",EDGE,{"disambiguationData":[OSD([subQ3,subQ2,subQ1,subQ0])],"isStart":true})]})])],"isStart":false});}
            var Q3;
            {var subQ0=sQuery(id+"F0.wireOp",EDGE,"E30");var subQ1=sQuery(id+"F0.wireOp",EDGE,"E20");var subQ2=sQuery(id+"F0.wireOp",EDGE,"E19");var subQ3=sQuery(id+"F0.wireOp",EDGE,"E18.top");Q3=makeQuery(id+"F15.opExtrude","CAP_EDGE",EDGE,{"disambiguationData":[OSD([subQ3,subQ2,subQ1,subQ0]),TDD([makeQuery(id+"F11.boolean.opBoolean","MERGE",EDGE,{"derivedFrom":[makeQuery(id+"F10.opChamfer","BLEND_EDGE",EDGE,{"blendedFrom":[makeQuery(id+"F3.opExtrude","CAP_EDGE",EDGE,{"disambiguationData":[OSD([subQ2]),TDD([makeQuery(id+"F0.imprint","IMPRINT",EDGE,{"disambiguationData":[TD([[makeQuery(id+"F0.imprint","INTERSECT",VERTEX,{"derivedFrom":[subQ3,subQ2]}),-1.0]])],"derivedFrom":subQ2})])],"isStart":false}),makeQuery(id+"F3.opExtrude","CAP_FACE",FACE,{"disambiguationData":[OSD([subQ3,subQ2,subQ1,subQ0])],"isStart":false})],"blendedInto":[makeQuery(id+"F3.opExtrude","CAP_FACE",FACE,{"disambiguationData":[OSD([subQ3,subQ2,subQ1,subQ0])],"isStart":false})]}),makeQuery(id+"F11.opExtrude","CAP_EDGE",EDGE,{"disambiguationData":[OSD([subQ3,subQ2,subQ1,subQ0])],"isStart":true})]})])],"isStart":false});}
            chamfer(context, id + "F17", {"entities" : qUnion([Q0, Q1, Q2, Q3]), "chamferType" : ChamferType.TWO_OFFSETS, "width1" : 2 * mm, "oppositeDirection" : false, "width2" : 10 * mm, "tangentPropagation" : true});
        }
        {
            var Q0;
            {var subQ0=sQuery(id+"F0.wireOp",EDGE,"E18.bottom");var subQ2=sQuery(id+"F0.wireOp",EDGE,"E19");var subQ3=makeQuery(id+"F0.imprint","IMPRINT",EDGE,{"disambiguationData":[TD([[makeQuery(id+"F0.imprint","INTERSECT",VERTEX,{"derivedFrom":[subQ0,subQ2]}),1.0]])],"derivedFrom":subQ2});var subQ4=sQuery(id+"F5.wireOp",EDGE,"E46.top");Q0=makeQuery(id+"F13.opChamfer","BLEND_FACE",FACE,{"disambiguationData":[OSD([subQ2,subQ4]),TDD([makeQuery(id+"F12.opExtrude","CAP_EDGE",EDGE,{"disambiguationData":[OSD([subQ2,subQ4]),TDD([makeQuery(id+"F11.opExtrude","CAP_EDGE",EDGE,{"disambiguationData":[OSD([subQ2,subQ4]),TDD([makeQuery(id+"F10.opChamfer","BLEND_EDGE",EDGE,{"blendedFrom":[makeQuery(id+"F3.opExtrude","CAP_EDGE",EDGE,{"disambiguationData":[OSD([subQ2]),TDD([subQ3])],"isStart":false}),makeQuery(id+"F6.boolean.opBoolean","COPY",FACE,{"disambiguationData":[TD([makeQuery(id+"F2.opExtrude","SWEPT_FACE",FACE,{"disambiguationData":[OSD([subQ0])]})])],"derivedFrom":makeQuery(id+"F6.opExtrude","SWEPT_FACE",FACE,{"disambiguationData":[OSD([subQ4])]})})],"blendedInto":[makeQuery(id+"F6.boolean.opBoolean","COPY",FACE,{"disambiguationData":[TD([makeQuery(id+"F2.opExtrude","SWEPT_FACE",FACE,{"disambiguationData":[OSD([subQ0])]})])],"derivedFrom":makeQuery(id+"F6.opExtrude","SWEPT_FACE",FACE,{"disambiguationData":[OSD([subQ4])]})})]})])],"isStart":false})])],"isStart":false})])]});}
            var Q1;
            {var subQ0=sQuery(id+"F0.wireOp",EDGE,"E24");var subQ1=sQuery(id+"F0.wireOp",EDGE,"E19");var subQ3=makeQuery(id+"F0.imprint","IMPRINT",EDGE,{"disambiguationData":[TD([[makeQuery(id+"F0.imprint","INTERSECT",VERTEX,{"derivedFrom":[subQ1,subQ0]}),-1.0]])],"derivedFrom":subQ1});var subQ4=sQuery(id+"F5.wireOp",EDGE,"E46.top");Q1=makeQuery(id+"F13.opChamfer","BLEND_FACE",FACE,{"disambiguationData":[OSD([subQ1,subQ4]),TDD([makeQuery(id+"F12.opExtrude","CAP_EDGE",EDGE,{"disambiguationData":[OSD([subQ1,subQ4]),TDD([makeQuery(id+"F11.opExtrude","CAP_EDGE",EDGE,{"disambiguationData":[OSD([subQ1,subQ4]),TDD([makeQuery(id+"F10.opChamfer","BLEND_EDGE",EDGE,{"blendedFrom":[makeQuery(id+"F3.opExtrude","CAP_EDGE",EDGE,{"disambiguationData":[OSD([subQ1]),TDD([subQ3])],"isStart":false}),makeQuery(id+"F6.boolean.opBoolean","COPY",FACE,{"disambiguationData":[TD([makeQuery(id+"F2.opExtrude","SWEPT_FACE",FACE,{"disambiguationData":[OSD([subQ0])]})])],"derivedFrom":makeQuery(id+"F6.opExtrude","SWEPT_FACE",FACE,{"disambiguationData":[OSD([subQ4])]})})],"blendedInto":[makeQuery(id+"F6.boolean.opBoolean","COPY",FACE,{"disambiguationData":[TD([makeQuery(id+"F2.opExtrude","SWEPT_FACE",FACE,{"disambiguationData":[OSD([subQ0])]})])],"derivedFrom":makeQuery(id+"F6.opExtrude","SWEPT_FACE",FACE,{"disambiguationData":[OSD([subQ4])]})})]})])],"isStart":false})])],"isStart":false})])]});}
            extrude(context, id + "F18", {"entities" : qUnion([Q0, Q1]), "operationType" : NewBodyOperationType.ADD, "oppositeDirection" : true, "depth" : 1 * mm});
        }
        {
            var Q0;
            {var subQ0=sQuery(id+"F0.wireOp",EDGE,"E19");var subQ1=sQuery(id+"F0.wireOp",EDGE,"E18.bottom");var subQ3=makeQuery(id+"F0.imprint","IMPRINT",EDGE,{"disambiguationData":[TD([[makeQuery(id+"F0.imprint","INTERSECT",VERTEX,{"derivedFrom":[subQ1,subQ0]}),1.0]])],"derivedFrom":subQ0});var subQ4=makeQuery(id+"F3.opExtrude","CAP_EDGE",EDGE,{"disambiguationData":[OSD([subQ0]),TDD([subQ3])],"isStart":false});var subQ5=sQuery(id+"F5.wireOp",EDGE,"E46.top");Q0=makeQuery(id+"F13.opChamfer","BLEND_EDGE",EDGE,{"blendedFrom":[makeQuery(id+"F12.opExtrude","CAP_EDGE",EDGE,{"disambiguationData":[OSD([subQ0,subQ5]),TDD([makeQuery(id+"F11.opExtrude","CAP_EDGE",EDGE,{"disambiguationData":[OSD([subQ0,subQ5]),TDD([makeQuery(id+"F10.opChamfer","BLEND_EDGE",EDGE,{"blendedFrom":[subQ4,makeQuery(id+"F6.boolean.opBoolean","COPY",FACE,{"disambiguationData":[TD([makeQuery(id+"F2.opExtrude","SWEPT_FACE",FACE,{"disambiguationData":[OSD([subQ1])]})])],"derivedFrom":makeQuery(id+"F6.opExtrude","SWEPT_FACE",FACE,{"disambiguationData":[OSD([subQ5])]})})],"blendedInto":[makeQuery(id+"F6.boolean.opBoolean","COPY",FACE,{"disambiguationData":[TD([makeQuery(id+"F2.opExtrude","SWEPT_FACE",FACE,{"disambiguationData":[OSD([subQ1])]})])],"derivedFrom":makeQuery(id+"F6.opExtrude","SWEPT_FACE",FACE,{"disambiguationData":[OSD([subQ5])]})})]})])],"isStart":false})])],"isStart":false}),makeQuery(id+"F12.opExtrude","CAP_FACE",FACE,{"disambiguationData":[OSD([subQ0]),TDD([makeQuery(id+"F11.opExtrude","CAP_FACE",FACE,{"disambiguationData":[OSD([subQ0]),TDD([makeQuery(id+"F10.opChamfer","BLEND_FACE",FACE,{"disambiguationData":[OSD([subQ0]),TDD([subQ4])]})])],"isStart":false})])],"isStart":false})],"blendedInto":[makeQuery(id+"F12.opExtrude","CAP_FACE",FACE,{"disambiguationData":[OSD([subQ0]),TDD([makeQuery(id+"F11.opExtrude","CAP_FACE",FACE,{"disambiguationData":[OSD([subQ0]),TDD([makeQuery(id+"F10.opChamfer","BLEND_FACE",FACE,{"disambiguationData":[OSD([subQ0]),TDD([subQ4])]})])],"isStart":false})])],"isStart":false})]});}
            var Q1;
            {var subQ0=sQuery(id+"F0.wireOp",EDGE,"E24");var subQ1=sQuery(id+"F0.wireOp",EDGE,"E19");var subQ3=makeQuery(id+"F0.imprint","IMPRINT",EDGE,{"disambiguationData":[TD([[makeQuery(id+"F0.imprint","INTERSECT",VERTEX,{"derivedFrom":[subQ1,subQ0]}),-1.0]])],"derivedFrom":subQ1});var subQ4=makeQuery(id+"F3.opExtrude","CAP_EDGE",EDGE,{"disambiguationData":[OSD([subQ1]),TDD([subQ3])],"isStart":false});var subQ5=sQuery(id+"F5.wireOp",EDGE,"E46.top");Q1=makeQuery(id+"F13.opChamfer","BLEND_EDGE",EDGE,{"blendedFrom":[makeQuery(id+"F12.opExtrude","CAP_EDGE",EDGE,{"disambiguationData":[OSD([subQ1,subQ5]),TDD([makeQuery(id+"F11.opExtrude","CAP_EDGE",EDGE,{"disambiguationData":[OSD([subQ1,subQ5]),TDD([makeQuery(id+"F10.opChamfer","BLEND_EDGE",EDGE,{"blendedFrom":[subQ4,makeQuery(id+"F6.boolean.opBoolean","COPY",FACE,{"disambiguationData":[TD([makeQuery(id+"F2.opExtrude","SWEPT_FACE",FACE,{"disambiguationData":[OSD([subQ0])]})])],"derivedFrom":makeQuery(id+"F6.opExtrude","SWEPT_FACE",FACE,{"disambiguationData":[OSD([subQ5])]})})],"blendedInto":[makeQuery(id+"F6.boolean.opBoolean","COPY",FACE,{"disambiguationData":[TD([makeQuery(id+"F2.opExtrude","SWEPT_FACE",FACE,{"disambiguationData":[OSD([subQ0])]})])],"derivedFrom":makeQuery(id+"F6.opExtrude","SWEPT_FACE",FACE,{"disambiguationData":[OSD([subQ5])]})})]})])],"isStart":false})])],"isStart":false}),makeQuery(id+"F12.opExtrude","CAP_FACE",FACE,{"disambiguationData":[OSD([subQ1]),TDD([makeQuery(id+"F11.opExtrude","CAP_FACE",FACE,{"disambiguationData":[OSD([subQ1]),TDD([makeQuery(id+"F10.opChamfer","BLEND_FACE",FACE,{"disambiguationData":[OSD([subQ1]),TDD([subQ4])]})])],"isStart":false})])],"isStart":false})],"blendedInto":[makeQuery(id+"F12.opExtrude","CAP_FACE",FACE,{"disambiguationData":[OSD([subQ1]),TDD([makeQuery(id+"F11.opExtrude","CAP_FACE",FACE,{"disambiguationData":[OSD([subQ1]),TDD([makeQuery(id+"F10.opChamfer","BLEND_FACE",FACE,{"disambiguationData":[OSD([subQ1]),TDD([subQ4])]})])],"isStart":false})])],"isStart":false})]});}
            var Q2;
            Q2=makeQuery(id+"F4.opExtrude","CAP_EDGE",EDGE,{"disambiguationData":[OSD([sQuery(id+"F0.wireOp",EDGE,"E18.right")])],"isStart":false});
            var Q3;
            {var subQ0=sQuery(id+"F0.wireOp",EDGE,"E18.right");Q3=makeQuery(id+"F9.opChamfer","BLEND_EDGE",EDGE,{"blendedFrom":[makeQuery(id+"F4.opExtrude","CAP_EDGE",EDGE,{"disambiguationData":[OSD([subQ0])],"isStart":true}),makeQuery(id+"F4.opExtrude","SWEPT_FACE",FACE,{"disambiguationData":[OSD([subQ0])]})],"blendedInto":[makeQuery(id+"F4.opExtrude","SWEPT_FACE",FACE,{"disambiguationData":[OSD([subQ0])]})]});}
            fillet(context, id + "F19", {"entities" : qUnion([Q0, Q1, Q2, Q3]), "radius" : 1 * mm, "allowEdgeOverflow" : false});
        }
        {
            var Q0;
            {var subQ0=sQuery(id+"F0.wireOp",EDGE,"E27");var subQ1=sQuery(id+"F0.wireOp",EDGE,"E20");var subQ2=sQuery(id+"F0.wireOp",EDGE,"E19");var subQ3=sQuery(id+"F0.wireOp",EDGE,"E18.bottom");var subQ4=makeQuery(id+"F10.opChamfer","BLEND_VERTEX",VERTEX,{"blendedFrom":[makeQuery(id+"F3.opExtrude","CAP_EDGE",EDGE,{"disambiguationData":[OSD([subQ2]),TDD([makeQuery(id+"F0.imprint","IMPRINT",EDGE,{"disambiguationData":[TD([[makeQuery(id+"F0.imprint","INTERSECT",VERTEX,{"derivedFrom":[subQ3,subQ2]}),1.0]])],"derivedFrom":subQ2})])],"isStart":false}),makeQuery(id+"F3.opExtrude","CAP_FACE",FACE,{"disambiguationData":[OSD([subQ3,subQ2,subQ1,subQ0])],"isStart":false}),makeQuery(id+"F3.boolean.opBoolean","MERGE",FACE,{"derivedFrom":[makeQuery(id+"F2.opExtrude","SWEPT_FACE",FACE,{"disambiguationData":[OSD([subQ0])]}),makeQuery(id+"F3.opExtrude","SWEPT_FACE",FACE,{"disambiguationData":[OSD([subQ0])]})]})],"blendedInto":[makeQuery(id+"F3.opExtrude","CAP_FACE",FACE,{"disambiguationData":[OSD([subQ3,subQ2,subQ1,subQ0])],"isStart":false}),makeQuery(id+"F3.boolean.opBoolean","MERGE",FACE,{"derivedFrom":[makeQuery(id+"F2.opExtrude","SWEPT_FACE",FACE,{"disambiguationData":[OSD([subQ0])]}),makeQuery(id+"F3.opExtrude","SWEPT_FACE",FACE,{"disambiguationData":[OSD([subQ0])]})]})]});Q0=makeQuery(id+"F15.opExtrude","CAP_EDGE",EDGE,{"disambiguationData":[OSD([subQ3,subQ2,subQ1,subQ0]),TDD([makeQuery(id+"F12.boolean.opBoolean","MERGE",EDGE,{"derivedFrom":[makeQuery(id+"F11.opExtrude","SWEPT_EDGE",EDGE,{"disambiguationData":[OSD([subQ3,subQ2,subQ1,subQ0]),TDD([subQ4])]}),makeQuery(id+"F12.opExtrude","SWEPT_EDGE",EDGE,{"disambiguationData":[OSD([subQ3,subQ2,subQ1,subQ0]),TDD([makeQuery(id+"F11.opExtrude","CAP_VERTEX",VERTEX,{"disambiguationData":[OSD([subQ3,subQ2,subQ1,subQ0]),TDD([subQ4])],"isStart":false})])]})]})])],"isStart":false});}
            var Q1;
            {var subQ0=sQuery(id+"F0.wireOp",EDGE,"E25");var subQ1=sQuery(id+"F0.wireOp",EDGE,"E24");var subQ2=sQuery(id+"F0.wireOp",EDGE,"E20");var subQ3=sQuery(id+"F0.wireOp",EDGE,"E19");var subQ4=makeQuery(id+"F10.opChamfer","BLEND_VERTEX",VERTEX,{"blendedFrom":[makeQuery(id+"F3.opExtrude","CAP_EDGE",EDGE,{"disambiguationData":[OSD([subQ3]),TDD([makeQuery(id+"F0.imprint","IMPRINT",EDGE,{"disambiguationData":[TD([[makeQuery(id+"F0.imprint","INTERSECT",VERTEX,{"derivedFrom":[subQ3,subQ1]}),-1.0]])],"derivedFrom":subQ3})])],"isStart":false}),makeQuery(id+"F3.opExtrude","CAP_FACE",FACE,{"disambiguationData":[OSD([subQ3,subQ2,subQ1,subQ0])],"isStart":false}),makeQuery(id+"F3.boolean.opBoolean","MERGE",FACE,{"derivedFrom":[makeQuery(id+"F2.opExtrude","SWEPT_FACE",FACE,{"disambiguationData":[OSD([subQ0])]}),makeQuery(id+"F3.opExtrude","SWEPT_FACE",FACE,{"disambiguationData":[OSD([subQ0])]})]})],"blendedInto":[makeQuery(id+"F3.opExtrude","CAP_FACE",FACE,{"disambiguationData":[OSD([subQ3,subQ2,subQ1,subQ0])],"isStart":false}),makeQuery(id+"F3.boolean.opBoolean","MERGE",FACE,{"derivedFrom":[makeQuery(id+"F2.opExtrude","SWEPT_FACE",FACE,{"disambiguationData":[OSD([subQ0])]}),makeQuery(id+"F3.opExtrude","SWEPT_FACE",FACE,{"disambiguationData":[OSD([subQ0])]})]})]});Q1=makeQuery(id+"F15.opExtrude","CAP_EDGE",EDGE,{"disambiguationData":[OSD([subQ3,subQ2,subQ1,subQ0]),TDD([makeQuery(id+"F12.boolean.opBoolean","MERGE",EDGE,{"derivedFrom":[makeQuery(id+"F11.opExtrude","SWEPT_EDGE",EDGE,{"disambiguationData":[OSD([subQ3,subQ2,subQ1,subQ0]),TDD([subQ4])]}),makeQuery(id+"F12.opExtrude","SWEPT_EDGE",EDGE,{"disambiguationData":[OSD([subQ3,subQ2,subQ1,subQ0]),TDD([makeQuery(id+"F11.opExtrude","CAP_VERTEX",VERTEX,{"disambiguationData":[OSD([subQ3,subQ2,subQ1,subQ0]),TDD([subQ4])],"isStart":false})])]})]})])],"isStart":false});}
            var Q2;
            {var subQ0=sQuery(id+"F0.wireOp",EDGE,"E24");var subQ1=sQuery(id+"F0.wireOp",EDGE,"E25");var subQ2=sQuery(id+"F0.wireOp",EDGE,"E20");var subQ3=sQuery(id+"F0.wireOp",EDGE,"E19");var subQ4=makeQuery(id+"F10.opChamfer","BLEND_VERTEX",VERTEX,{"blendedFrom":[makeQuery(id+"F3.opExtrude","CAP_EDGE",EDGE,{"disambiguationData":[OSD([subQ3]),TDD([makeQuery(id+"F0.imprint","IMPRINT",EDGE,{"disambiguationData":[TD([[makeQuery(id+"F0.imprint","INTERSECT",VERTEX,{"derivedFrom":[subQ3,subQ0]}),-1.0]])],"derivedFrom":subQ3})])],"isStart":false}),makeQuery(id+"F3.opExtrude","CAP_FACE",FACE,{"disambiguationData":[OSD([subQ3,subQ2,subQ0,subQ1])],"isStart":false}),makeQuery(id+"F3.boolean.opBoolean","MERGE",FACE,{"derivedFrom":[makeQuery(id+"F2.opExtrude","SWEPT_FACE",FACE,{"disambiguationData":[OSD([subQ0])]}),makeQuery(id+"F3.opExtrude","SWEPT_FACE",FACE,{"disambiguationData":[OSD([subQ0])]})]})],"blendedInto":[makeQuery(id+"F3.opExtrude","CAP_FACE",FACE,{"disambiguationData":[OSD([subQ3,subQ2,subQ0,subQ1])],"isStart":false}),makeQuery(id+"F3.boolean.opBoolean","MERGE",FACE,{"derivedFrom":[makeQuery(id+"F2.opExtrude","SWEPT_FACE",FACE,{"disambiguationData":[OSD([subQ0])]}),makeQuery(id+"F3.opExtrude","SWEPT_FACE",FACE,{"disambiguationData":[OSD([subQ0])]})]})]});Q2=makeQuery(id+"F15.opExtrude","CAP_EDGE",EDGE,{"disambiguationData":[OSD([subQ3,subQ2,subQ0,subQ1]),TDD([makeQuery(id+"F12.boolean.opBoolean","MERGE",EDGE,{"derivedFrom":[makeQuery(id+"F11.opExtrude","SWEPT_EDGE",EDGE,{"disambiguationData":[OSD([subQ3,subQ2,subQ0,subQ1]),TDD([subQ4])]}),makeQuery(id+"F12.opExtrude","SWEPT_EDGE",EDGE,{"disambiguationData":[OSD([subQ3,subQ2,subQ0,subQ1]),TDD([makeQuery(id+"F11.opExtrude","CAP_VERTEX",VERTEX,{"disambiguationData":[OSD([subQ3,subQ2,subQ0,subQ1]),TDD([subQ4])],"isStart":false})])]})]})])],"isStart":false});}
            var Q3;
            {var subQ0=sQuery(id+"F0.wireOp",EDGE,"E22");var subQ1=sQuery(id+"F0.wireOp",EDGE,"E28");var subQ2=sQuery(id+"F0.wireOp",EDGE,"E20");var subQ3=sQuery(id+"F0.wireOp",EDGE,"E19");var subQ4=makeQuery(id+"F10.opChamfer","BLEND_VERTEX",VERTEX,{"blendedFrom":[makeQuery(id+"F3.opExtrude","CAP_EDGE",EDGE,{"disambiguationData":[OSD([subQ3]),TDD([makeQuery(id+"F0.imprint","IMPRINT",EDGE,{"disambiguationData":[TD([[makeQuery(id+"F0.imprint","INTERSECT",VERTEX,{"derivedFrom":[subQ3,subQ1]}),-1.0]])],"derivedFrom":subQ3})])],"isStart":false}),makeQuery(id+"F3.opExtrude","CAP_FACE",FACE,{"disambiguationData":[OSD([subQ3,subQ2,subQ0,subQ1])],"isStart":false}),makeQuery(id+"F3.boolean.opBoolean","MERGE",FACE,{"derivedFrom":[makeQuery(id+"F2.opExtrude","SWEPT_FACE",FACE,{"disambiguationData":[OSD([subQ0])]}),makeQuery(id+"F3.opExtrude","SWEPT_FACE",FACE,{"disambiguationData":[OSD([subQ0])]})]})],"blendedInto":[makeQuery(id+"F3.opExtrude","CAP_FACE",FACE,{"disambiguationData":[OSD([subQ3,subQ2,subQ0,subQ1])],"isStart":false}),makeQuery(id+"F3.boolean.opBoolean","MERGE",FACE,{"derivedFrom":[makeQuery(id+"F2.opExtrude","SWEPT_FACE",FACE,{"disambiguationData":[OSD([subQ0])]}),makeQuery(id+"F3.opExtrude","SWEPT_FACE",FACE,{"disambiguationData":[OSD([subQ0])]})]})]});Q3=makeQuery(id+"F15.opExtrude","CAP_EDGE",EDGE,{"disambiguationData":[OSD([subQ3,subQ2,subQ0,subQ1]),TDD([makeQuery(id+"F12.boolean.opBoolean","MERGE",EDGE,{"derivedFrom":[makeQuery(id+"F11.opExtrude","SWEPT_EDGE",EDGE,{"disambiguationData":[OSD([subQ3,subQ2,subQ0,subQ1]),TDD([subQ4])]}),makeQuery(id+"F12.opExtrude","SWEPT_EDGE",EDGE,{"disambiguationData":[OSD([subQ3,subQ2,subQ0,subQ1]),TDD([makeQuery(id+"F11.opExtrude","CAP_VERTEX",VERTEX,{"disambiguationData":[OSD([subQ3,subQ2,subQ0,subQ1]),TDD([subQ4])],"isStart":false})])]})]})])],"isStart":false});}
            var Q4;
            {var subQ0=sQuery(id+"F0.wireOp",EDGE,"E28");var subQ1=sQuery(id+"F0.wireOp",EDGE,"E22");var subQ2=sQuery(id+"F0.wireOp",EDGE,"E20");var subQ3=sQuery(id+"F0.wireOp",EDGE,"E19");var subQ4=makeQuery(id+"F10.opChamfer","BLEND_VERTEX",VERTEX,{"blendedFrom":[makeQuery(id+"F3.opExtrude","CAP_EDGE",EDGE,{"disambiguationData":[OSD([subQ3]),TDD([makeQuery(id+"F0.imprint","IMPRINT",EDGE,{"disambiguationData":[TD([[makeQuery(id+"F0.imprint","INTERSECT",VERTEX,{"derivedFrom":[subQ3,subQ0]}),-1.0]])],"derivedFrom":subQ3})])],"isStart":false}),makeQuery(id+"F3.opExtrude","CAP_FACE",FACE,{"disambiguationData":[OSD([subQ3,subQ2,subQ1,subQ0])],"isStart":false}),makeQuery(id+"F3.boolean.opBoolean","MERGE",FACE,{"derivedFrom":[makeQuery(id+"F2.opExtrude","SWEPT_FACE",FACE,{"disambiguationData":[OSD([subQ0])]}),makeQuery(id+"F3.opExtrude","SWEPT_FACE",FACE,{"disambiguationData":[OSD([subQ0])]})]})],"blendedInto":[makeQuery(id+"F3.opExtrude","CAP_FACE",FACE,{"disambiguationData":[OSD([subQ3,subQ2,subQ1,subQ0])],"isStart":false}),makeQuery(id+"F3.boolean.opBoolean","MERGE",FACE,{"derivedFrom":[makeQuery(id+"F2.opExtrude","SWEPT_FACE",FACE,{"disambiguationData":[OSD([subQ0])]}),makeQuery(id+"F3.opExtrude","SWEPT_FACE",FACE,{"disambiguationData":[OSD([subQ0])]})]})]});Q4=makeQuery(id+"F15.opExtrude","CAP_EDGE",EDGE,{"disambiguationData":[OSD([subQ3,subQ2,subQ1,subQ0]),TDD([makeQuery(id+"F12.boolean.opBoolean","MERGE",EDGE,{"derivedFrom":[makeQuery(id+"F11.opExtrude","SWEPT_EDGE",EDGE,{"disambiguationData":[OSD([subQ3,subQ2,subQ1,subQ0]),TDD([subQ4])]}),makeQuery(id+"F12.opExtrude","SWEPT_EDGE",EDGE,{"disambiguationData":[OSD([subQ3,subQ2,subQ1,subQ0]),TDD([makeQuery(id+"F11.opExtrude","CAP_VERTEX",VERTEX,{"disambiguationData":[OSD([subQ3,subQ2,subQ1,subQ0]),TDD([subQ4])],"isStart":false})])]})]})])],"isStart":false});}
            var Q5;
            {var subQ0=sQuery(id+"F0.wireOp",EDGE,"E30");var subQ1=sQuery(id+"F0.wireOp",EDGE,"E20");var subQ2=sQuery(id+"F0.wireOp",EDGE,"E19");var subQ3=sQuery(id+"F0.wireOp",EDGE,"E18.top");var subQ4=makeQuery(id+"F10.opChamfer","BLEND_VERTEX",VERTEX,{"blendedFrom":[makeQuery(id+"F3.opExtrude","CAP_EDGE",EDGE,{"disambiguationData":[OSD([subQ2]),TDD([makeQuery(id+"F0.imprint","IMPRINT",EDGE,{"disambiguationData":[TD([[makeQuery(id+"F0.imprint","INTERSECT",VERTEX,{"derivedFrom":[subQ3,subQ2]}),-1.0]])],"derivedFrom":subQ2})])],"isStart":false}),makeQuery(id+"F3.opExtrude","CAP_FACE",FACE,{"disambiguationData":[OSD([subQ3,subQ2,subQ1,subQ0])],"isStart":false}),makeQuery(id+"F3.boolean.opBoolean","MERGE",FACE,{"derivedFrom":[makeQuery(id+"F2.opExtrude","SWEPT_FACE",FACE,{"disambiguationData":[OSD([subQ0])]}),makeQuery(id+"F3.opExtrude","SWEPT_FACE",FACE,{"disambiguationData":[OSD([subQ0])]})]})],"blendedInto":[makeQuery(id+"F3.opExtrude","CAP_FACE",FACE,{"disambiguationData":[OSD([subQ3,subQ2,subQ1,subQ0])],"isStart":false}),makeQuery(id+"F3.boolean.opBoolean","MERGE",FACE,{"derivedFrom":[makeQuery(id+"F2.opExtrude","SWEPT_FACE",FACE,{"disambiguationData":[OSD([subQ0])]}),makeQuery(id+"F3.opExtrude","SWEPT_FACE",FACE,{"disambiguationData":[OSD([subQ0])]})]})]});Q5=makeQuery(id+"F15.opExtrude","CAP_EDGE",EDGE,{"disambiguationData":[OSD([subQ3,subQ2,subQ1,subQ0]),TDD([makeQuery(id+"F12.boolean.opBoolean","MERGE",EDGE,{"derivedFrom":[makeQuery(id+"F11.opExtrude","SWEPT_EDGE",EDGE,{"disambiguationData":[OSD([subQ3,subQ2,subQ1,subQ0]),TDD([subQ4])]}),makeQuery(id+"F12.opExtrude","SWEPT_EDGE",EDGE,{"disambiguationData":[OSD([subQ3,subQ2,subQ1,subQ0]),TDD([makeQuery(id+"F11.opExtrude","CAP_VERTEX",VERTEX,{"disambiguationData":[OSD([subQ3,subQ2,subQ1,subQ0]),TDD([subQ4])],"isStart":false})])]})]})])],"isStart":false});}
            chamfer(context, id + "F20", {"entities" : qUnion([Q0, Q1, Q2, Q3, Q4, Q5]), "width" : 1 * mm});
        }
        {
            var Q0;
            Q0=makeQuery(id+"F1.opExtrude","SWEPT_EDGE",EDGE,{"disambiguationData":[OSD([sQuery(id+"F0.wireOp",EDGE,"sCiXkZ15-kqQ6-fgVC-MlON-RFexCfodkABL.top"),sQuery(id+"F0.wireOp",EDGE,"sCiXkZ15-kqQ6-fgVC-MlON-RFexCfodkABL.right")])]});
            var Q1;
            Q1=makeQuery(id+"F1.opExtrude","SWEPT_EDGE",EDGE,{"disambiguationData":[OSD([sQuery(id+"F0.wireOp",EDGE,"sCiXkZ15-kqQ6-fgVC-MlON-RFexCfodkABL.bottom"),sQuery(id+"F0.wireOp",EDGE,"sCiXkZ15-kqQ6-fgVC-MlON-RFexCfodkABL.right")])]});
            var Q2;
            Q2=makeQuery(id+"F1.opExtrude","SWEPT_EDGE",EDGE,{"disambiguationData":[OSD([sQuery(id+"F0.wireOp",EDGE,"rwhcs4uc-SkOH-cghl-mAYi-ZJsiErxD8eiY.left"),sQuery(id+"F0.wireOp",EDGE,"sCiXkZ15-kqQ6-fgVC-MlON-RFexCfodkABL.bottom")])]});
            var Q3;
            Q3=makeQuery(id+"F1.opExtrude","SWEPT_EDGE",EDGE,{"disambiguationData":[OSD([sQuery(id+"F0.wireOp",EDGE,"sCiXkZ15-kqQ6-fgVC-MlON-RFexCfodkABL.top"),sQuery(id+"F0.wireOp",EDGE,"sCiXkZ15-kqQ6-fgVC-MlON-RFexCfodkABL.left")])]});
            var Q4;
            Q4=makeQuery(id+"F1.opExtrude","SWEPT_EDGE",EDGE,{"disambiguationData":[OSD([sQuery(id+"F0.wireOp",EDGE,"rwhcs4uc-SkOH-cghl-mAYi-ZJsiErxD8eiY.right"),sQuery(id+"F0.wireOp",EDGE,"sCiXkZ15-kqQ6-fgVC-MlON-RFexCfodkABL.bottom")])]});
            var Q5;
            Q5=makeQuery(id+"F1.opExtrude","SWEPT_EDGE",EDGE,{"disambiguationData":[OSD([sQuery(id+"F0.wireOp",EDGE,"E18.bottom"),sQuery(id+"F0.wireOp",EDGE,"rwhcs4uc-SkOH-cghl-mAYi-ZJsiErxD8eiY.bottom"),sQuery(id+"F0.wireOp",EDGE,"rwhcs4uc-SkOH-cghl-mAYi-ZJsiErxD8eiY.right")])]});
            var Q6;
            Q6=makeQuery(id+"F1.opExtrude","SWEPT_EDGE",EDGE,{"disambiguationData":[OSD([sQuery(id+"F0.wireOp",EDGE,"E18.bottom"),sQuery(id+"F0.wireOp",EDGE,"rwhcs4uc-SkOH-cghl-mAYi-ZJsiErxD8eiY.bottom"),sQuery(id+"F0.wireOp",EDGE,"rwhcs4uc-SkOH-cghl-mAYi-ZJsiErxD8eiY.left")])]});
            var Q7;
            Q7=makeQuery(id+"F1.opExtrude","SWEPT_EDGE",EDGE,{"disambiguationData":[OSD([sQuery(id+"F0.wireOp",EDGE,"sCiXkZ15-kqQ6-fgVC-MlON-RFexCfodkABL.bottom"),sQuery(id+"F0.wireOp",EDGE,"sCiXkZ15-kqQ6-fgVC-MlON-RFexCfodkABL.left")])]});
            var Q8;
            Q8=makeQuery(id+"F1.opExtrude","SWEPT_EDGE",EDGE,{"disambiguationData":[OSD([sQuery(id+"F0.wireOp",EDGE,"bATZT0iZ-d9cl-9QYs-YyeB-90eJ3BEw8Ait.bottom"),sQuery(id+"F0.wireOp",EDGE,"bATZT0iZ-d9cl-9QYs-YyeB-90eJ3BEw8Ait.right")])]});
            var Q9;
            Q9=makeQuery(id+"F1.opExtrude","SWEPT_EDGE",EDGE,{"disambiguationData":[OSD([sQuery(id+"F0.wireOp",EDGE,"E45.right"),sQuery(id+"F0.wireOp",EDGE,"bATZT0iZ-d9cl-9QYs-YyeB-90eJ3BEw8Ait.bottom")])]});
            var Q10;
            Q10=makeQuery(id+"F1.opExtrude","SWEPT_EDGE",EDGE,{"disambiguationData":[OSD([sQuery(id+"F0.wireOp",EDGE,"E18.bottom"),sQuery(id+"F0.wireOp",EDGE,"E45.bottom"),sQuery(id+"F0.wireOp",EDGE,"E45.right")])]});
            var Q11;
            Q11=makeQuery(id+"F1.opExtrude","SWEPT_EDGE",EDGE,{"disambiguationData":[OSD([sQuery(id+"F0.wireOp",EDGE,"E45.left"),sQuery(id+"F0.wireOp",EDGE,"bATZT0iZ-d9cl-9QYs-YyeB-90eJ3BEw8Ait.bottom")])]});
            var Q12;
            Q12=makeQuery(id+"F1.opExtrude","SWEPT_EDGE",EDGE,{"disambiguationData":[OSD([sQuery(id+"F0.wireOp",EDGE,"E18.bottom"),sQuery(id+"F0.wireOp",EDGE,"E45.bottom"),sQuery(id+"F0.wireOp",EDGE,"E45.left")])]});
            var Q13;
            Q13=makeQuery(id+"F1.opExtrude","SWEPT_EDGE",EDGE,{"disambiguationData":[OSD([sQuery(id+"F0.wireOp",EDGE,"bATZT0iZ-d9cl-9QYs-YyeB-90eJ3BEw8Ait.top"),sQuery(id+"F0.wireOp",EDGE,"bATZT0iZ-d9cl-9QYs-YyeB-90eJ3BEw8Ait.left")])]});
            var Q14;
            Q14=makeQuery(id+"F1.opExtrude","SWEPT_EDGE",EDGE,{"disambiguationData":[OSD([sQuery(id+"F0.wireOp",EDGE,"bATZT0iZ-d9cl-9QYs-YyeB-90eJ3BEw8Ait.top"),sQuery(id+"F0.wireOp",EDGE,"bATZT0iZ-d9cl-9QYs-YyeB-90eJ3BEw8Ait.right")])]});
            var Q15;
            Q15=makeQuery(id+"F1.opExtrude","SWEPT_EDGE",EDGE,{"disambiguationData":[OSD([sQuery(id+"F0.wireOp",EDGE,"bATZT0iZ-d9cl-9QYs-YyeB-90eJ3BEw8Ait.bottom"),sQuery(id+"F0.wireOp",EDGE,"bATZT0iZ-d9cl-9QYs-YyeB-90eJ3BEw8Ait.left")])]});
            var Q16;
            Q16=makeQuery(id+"F1.opExtrude","SWEPT_EDGE",EDGE,{"disambiguationData":[OSD([sQuery(id+"F0.wireOp",EDGE,"E44.top"),sQuery(id+"F0.wireOp",EDGE,"E44.left")])]});
            var Q17;
            Q17=makeQuery(id+"F1.opExtrude","SWEPT_EDGE",EDGE,{"disambiguationData":[OSD([sQuery(id+"F0.wireOp",EDGE,"E39.left"),sQuery(id+"F0.wireOp",EDGE,"E44.bottom")])]});
            var Q18;
            Q18=makeQuery(id+"F1.opExtrude","SWEPT_EDGE",EDGE,{"disambiguationData":[OSD([sQuery(id+"F0.wireOp",EDGE,"E18.top"),sQuery(id+"F0.wireOp",EDGE,"E39.bottom"),sQuery(id+"F0.wireOp",EDGE,"E39.left")])]});
            var Q19;
            Q19=makeQuery(id+"F1.opExtrude","SWEPT_EDGE",EDGE,{"disambiguationData":[OSD([sQuery(id+"F0.wireOp",EDGE,"E44.bottom"),sQuery(id+"F0.wireOp",EDGE,"E44.left")])]});
            var Q20;
            Q20=makeQuery(id+"F1.opExtrude","SWEPT_EDGE",EDGE,{"disambiguationData":[OSD([sQuery(id+"F0.wireOp",EDGE,"E44.bottom"),sQuery(id+"F0.wireOp",EDGE,"E44.right")])]});
            var Q21;
            Q21=makeQuery(id+"F1.opExtrude","SWEPT_EDGE",EDGE,{"disambiguationData":[OSD([sQuery(id+"F0.wireOp",EDGE,"E39.right"),sQuery(id+"F0.wireOp",EDGE,"E44.bottom")])]});
            var Q22;
            Q22=makeQuery(id+"F1.opExtrude","SWEPT_EDGE",EDGE,{"disambiguationData":[OSD([sQuery(id+"F0.wireOp",EDGE,"E18.top"),sQuery(id+"F0.wireOp",EDGE,"E39.bottom"),sQuery(id+"F0.wireOp",EDGE,"E39.right")])]});
            var Q23;
            Q23=makeQuery(id+"F1.opExtrude","SWEPT_EDGE",EDGE,{"disambiguationData":[OSD([sQuery(id+"F0.wireOp",EDGE,"E44.top"),sQuery(id+"F0.wireOp",EDGE,"E44.right")])]});
            var Q24;
            Q24=makeQuery(id+"F1.opExtrude","SWEPT_EDGE",EDGE,{"disambiguationData":[OSD([sQuery(id+"F0.wireOp",EDGE,"E43.top"),sQuery(id+"F0.wireOp",EDGE,"E43.right")])]});
            var Q25;
            Q25=makeQuery(id+"F1.opExtrude","SWEPT_EDGE",EDGE,{"disambiguationData":[OSD([sQuery(id+"F0.wireOp",EDGE,"E18.top"),sQuery(id+"F0.wireOp",EDGE,"E40.bottom"),sQuery(id+"F0.wireOp",EDGE,"E40.right")])]});
            var Q26;
            Q26=makeQuery(id+"F1.opExtrude","SWEPT_EDGE",EDGE,{"disambiguationData":[OSD([sQuery(id+"F0.wireOp",EDGE,"E40.right"),sQuery(id+"F0.wireOp",EDGE,"E43.bottom")])]});
            var Q27;
            Q27=makeQuery(id+"F1.opExtrude","SWEPT_EDGE",EDGE,{"disambiguationData":[OSD([sQuery(id+"F0.wireOp",EDGE,"E43.bottom"),sQuery(id+"F0.wireOp",EDGE,"E43.right")])]});
            var Q28;
            Q28=makeQuery(id+"F1.opExtrude","SWEPT_EDGE",EDGE,{"disambiguationData":[OSD([sQuery(id+"F0.wireOp",EDGE,"E40.left"),sQuery(id+"F0.wireOp",EDGE,"E43.bottom")])]});
            var Q29;
            Q29=makeQuery(id+"F1.opExtrude","SWEPT_EDGE",EDGE,{"disambiguationData":[OSD([sQuery(id+"F0.wireOp",EDGE,"E18.top"),sQuery(id+"F0.wireOp",EDGE,"E40.bottom"),sQuery(id+"F0.wireOp",EDGE,"E40.left")])]});
            var Q30;
            Q30=makeQuery(id+"F1.opExtrude","SWEPT_EDGE",EDGE,{"disambiguationData":[OSD([sQuery(id+"F0.wireOp",EDGE,"E43.top"),sQuery(id+"F0.wireOp",EDGE,"E43.left")])]});
            var Q31;
            Q31=makeQuery(id+"F1.opExtrude","SWEPT_EDGE",EDGE,{"disambiguationData":[OSD([sQuery(id+"F0.wireOp",EDGE,"E43.bottom"),sQuery(id+"F0.wireOp",EDGE,"E43.left")])]});
            fillet(context, id + "F21", {"entities" : qUnion([Q0, Q1, Q2, Q3, Q4, Q5, Q6, Q7, Q8, Q9, Q10, Q11, Q12, Q13, Q14, Q15, Q16, Q17, Q18, Q19, Q20, Q21, Q22, Q23, Q24, Q25, Q26, Q27, Q28, Q29, Q30, Q31]), "radius" : 1 * mm, "allowEdgeOverflow" : false});
        }
    });
